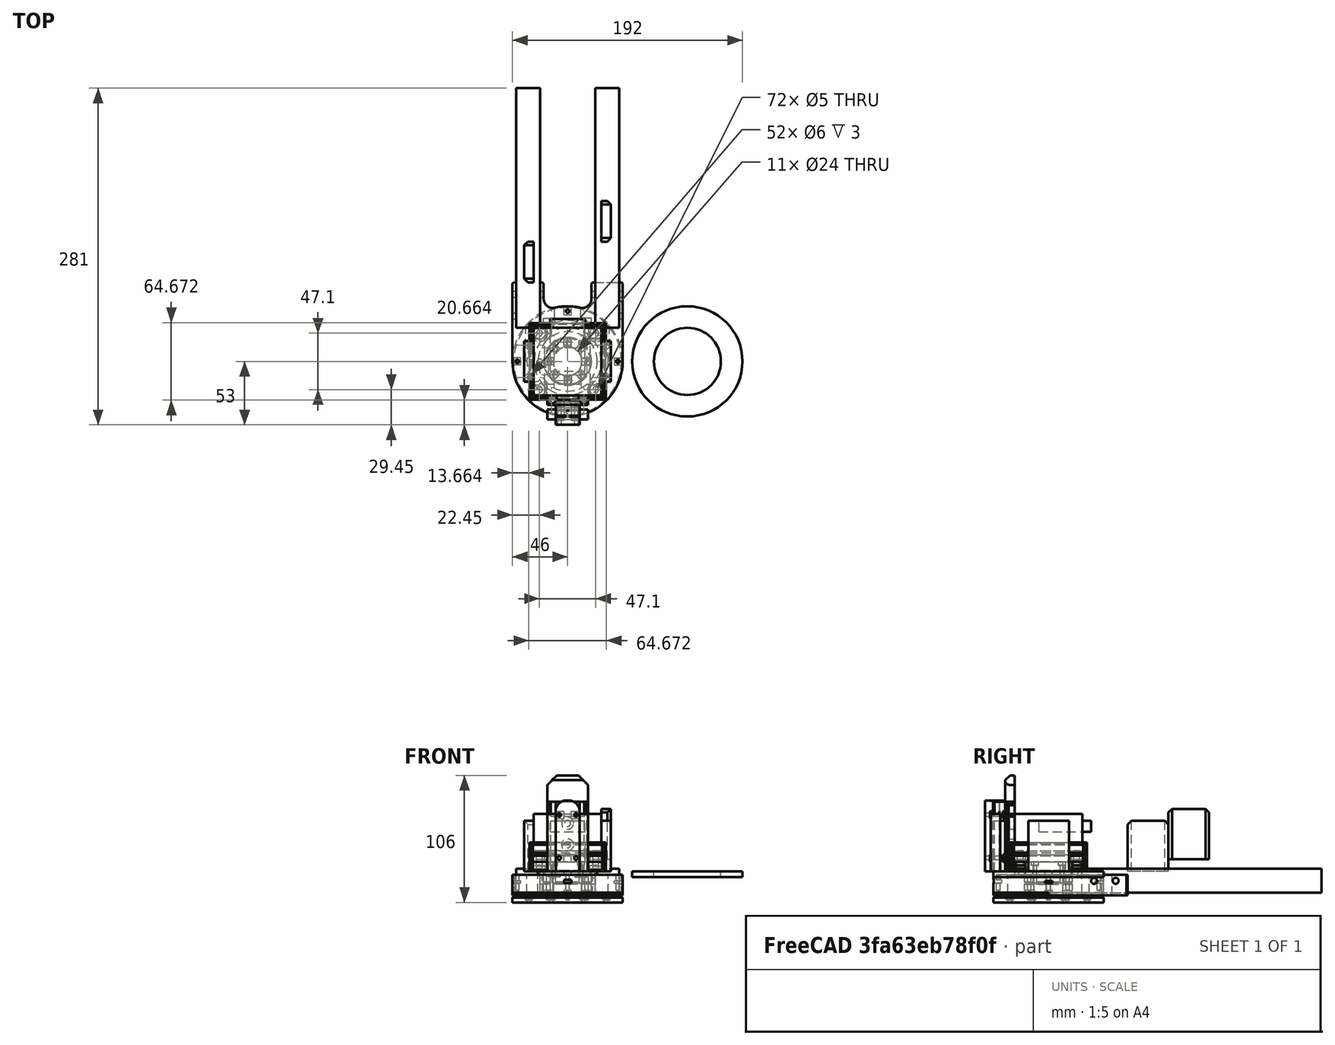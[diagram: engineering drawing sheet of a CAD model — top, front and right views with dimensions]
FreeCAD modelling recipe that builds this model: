
FCSTD DOCUMENT  (FreeCAD 0.19R24276 (Git))
Label: J-max_moto-hold_012
License: All rights reserved
LicenseURL: http://en.wikipedia.org/wiki/All_rights_reserved
objects: Part::Cylinder×298, Part::Box×162, Part::Compound×145, Part::Cut×126, Part::Chamfer×59, Part::FeaturePython×8, Mesh::Feature×7, Part::Fillet×7, Part::MultiFuse×3, Part::Mirroring×1, Part::Common×1
note: 810 computed .brp shape members not serialized (recipe doc carries the construction recipe); baked Part::Feature solids carry a one-line shape summary decoded from their .brp

FEATURE [Part::Cylinder] Cylinder116  label="Válec116"
  Angle = 360
  AttacherType = Attacher::AttachEngine3D
  Height = 20
  Placement = pos=(-13.3939,32.3358,-22) rot=(0,0,1;1.96349rad)
  Radius = 1.5
FEATURE [Part::Box] Box049  label="Krychle049"
  AttacherType = Attacher::AttachEngine3D
  Height = 2
  Length = 10
  Placement = pos=(-11,3,6) rot=(0,0,1;3.14159rad)
  Width = 6
FEATURE [Part::Cylinder] Cylinder127  label="Válec127"
  Angle = 360
  AttacherType = Attacher::AttachEngine3D
  Height = 3
  Placement = pos=(-32.3358,-13.3939,-22) rot=(0,0,1;3.53429rad)
  Radius = 3
FEATURE [Part::Cylinder] Cylinder124  label="Válec124"
  Angle = 360
  AttacherType = Attacher::AttachEngine3D
  Height = 3
  Placement = pos=(-32.3358,13.3939,-22) rot=(0,0,1;2.74889rad)
  Radius = 3
FEATURE [Part::Box] Box048  label="Krychle048"
  AttacherType = Attacher::AttachEngine3D
  Height = 2
  Length = 10
  Placement = pos=(3,11,6) rot=(0,0,1;1.5708rad)
  Width = 6
FEATURE [Part::Box] Box050  label="Krychle050"
  AttacherType = Attacher::AttachEngine3D
  Height = 2
  Length = 10
  Placement = pos=(-3,-11,6) rot=(0,0,-1;1.5708rad)
  Width = 6
FEATURE [Part::Cylinder] Cylinder131  label="Válec131"
  Angle = 360
  AttacherType = Attacher::AttachEngine3D
  Height = 16
  Placement = pos=(2e-15,16,2) rot=(0,0,-1;1.1781rad)
  Radius = 1.5
FEATURE [Part::Cylinder] Cylinder132  label="Válec132"
  Angle = 360
  AttacherType = Attacher::AttachEngine3D
  Height = 16
  Placement = pos=(-16,7e-15,2) rot=(0,0,1;0.392699rad)
  Radius = 1.5
FEATURE [Part::Cylinder] Cylinder126  label="Válec126"
  Angle = 360
  AttacherType = Attacher::AttachEngine3D
  Height = 3
  Placement = pos=(13.3939,-32.3358,-22) rot=(0,0,-1;1.1781rad)
  Radius = 3
FEATURE [Part::Cylinder] Cylinder130  label="Válec130"
  Angle = 360
  AttacherType = Attacher::AttachEngine3D
  Height = 16
  Placement = pos=(16,0,2) rot=(0,0,1;3.53429rad)
  Radius = 1.5
FEATURE [Part::Cylinder] Cylinder125  label="Válec125"
  Angle = 360
  AttacherType = Attacher::AttachEngine3D
  Height = 3
  Placement = pos=(-13.3939,-32.3358,-22) rot=(0,0,-1;1.96349rad)
  Radius = 3
FEATURE [Part::Cylinder] Cylinder128  label="Válec128"
  Angle = 360
  AttacherType = Attacher::AttachEngine3D
  Height = 3
  Placement = pos=(32.3358,13.3939,-22) rot=(0,0,1;0.392699rad)
  Radius = 3
FEATURE [Part::Cylinder] Cylinder129  label="Válec129"
  Angle = 360
  AttacherType = Attacher::AttachEngine3D
  Height = 3
  Placement = pos=(13.3939,32.3358,-22) rot=(0,0,1;1.1781rad)
  Radius = 3
FEATURE [Part::Box] Box  label="Krychle"
  AttacherType = Attacher::AttachEngine3D
  Height = 2
  Length = 10
  Placement = pos=(11,-3,6) rot=(0,0,1;0rad)
  Width = 6
FEATURE [Part::Cylinder] Cylinder122  label="Válec122"
  Angle = 360
  AttacherType = Attacher::AttachEngine3D
  Height = 3
  Placement = pos=(-13.3939,32.3358,-22) rot=(0,0,1;1.96349rad)
  Radius = 3
FEATURE [Part::Cylinder] Cylinder121  label="Válec121"
  Angle = 360
  AttacherType = Attacher::AttachEngine3D
  Height = 20
  Placement = pos=(32.3358,-13.3939,-22) rot=(0,0,-1;0.392699rad)
  Radius = 1.5
FEATURE [Part::Cylinder] Cylinder117  label="Válec117"
  Angle = 360
  AttacherType = Attacher::AttachEngine3D
  Height = 20
  Placement = pos=(-32.3358,13.3939,-22) rot=(0,0,1;2.74889rad)
  Radius = 1.5
FEATURE [Part::Cylinder] Cylinder123  label="Válec123"
  Angle = 360
  AttacherType = Attacher::AttachEngine3D
  Height = 3
  Placement = pos=(32.3358,-13.3939,-22) rot=(0,0,-1;0.392699rad)
  Radius = 3
FEATURE [Part::Cylinder] Cylinder119  label="Válec119"
  Angle = 360
  AttacherType = Attacher::AttachEngine3D
  Height = 20
  Placement = pos=(-13.3939,-32.3358,-22) rot=(0,0,-1;1.96349rad)
  Radius = 1.5
FEATURE [Part::Cylinder] Cylinder120  label="Válec120"
  Angle = 360
  AttacherType = Attacher::AttachEngine3D
  Height = 20
  Placement = pos=(13.3939,-32.3358,-22) rot=(0,0,-1;1.1781rad)
  Radius = 1.5
FEATURE [Part::Cylinder] Cylinder118  label="Válec118"
  Angle = 360
  AttacherType = Attacher::AttachEngine3D
  Height = 20
  Placement = pos=(-32.3358,-13.3939,-22) rot=(0,0,1;3.53429rad)
  Radius = 1.5
FEATURE [Part::FeaturePython] Tube009  # WARN: FeaturePython — macro-defined, semantics opaque (R4)
  AttacherType = Attacher::AttachEngine3D
  Height = 5
  InnerRadius = 12
  OuterRadius = 46
FEATURE [Part::FeaturePython] Tube010  # WARN: FeaturePython — macro-defined, semantics opaque (R4)
  AttacherType = Attacher::AttachEngine3D
  Height = 11
  InnerRadius = 12
  OuterRadius = 20
  Placement = pos=(0,0,5) rot=(0,0,1;0rad)
FEATURE [Part::Cylinder] Cylinder133  label="Válec133"
  Angle = 360
  AttacherType = Attacher::AttachEngine3D
  Height = 16
  Placement = pos=(-1.2e-14,-16,2) rot=(0,0,1;1.96349rad)
  Radius = 1.5
FEATURE [Part::Compound] Compound203
  Links = -> [Cylinder130,Cylinder131,Cylinder132,Cylinder133]
FEATURE [Part::Compound] Compound202
  Links = -> [Box,Box048,Box049,Box050]
  Placement = pos=(0,0,2) rot=(0,0,1;0rad)
FEATURE [Part::Cut] Cut
  Base = -> Tube010
  Tool = -> Compound202
FEATURE [Part::Compound] Compound204
  Links = -> [Tube009,Cut]
FEATURE [Part::Cylinder] Cylinder114  label="Válec114"
  Angle = 360
  AttacherType = Attacher::AttachEngine3D
  Height = 20
  Placement = pos=(32.3358,13.3939,-22) rot=(0,0,1;0.392699rad)
  Radius = 1.5
FEATURE [Part::Cylinder] Cylinder115  label="Válec115"
  Angle = 360
  AttacherType = Attacher::AttachEngine3D
  Height = 20
  Placement = pos=(13.3939,32.3358,-22) rot=(0,0,1;1.1781rad)
  Radius = 1.5
FEATURE [Part::Cut] Cut062
  Base = -> Compound204
  Tool = -> Compound203
FEATURE [Part::FeaturePython] Tube011  # WARN: FeaturePython — macro-defined, semantics opaque (R4)
  AttacherType = Attacher::AttachEngine3D
  Height = 3
  InnerRadius = 19
  OuterRadius = 24.8
  Placement = pos=(0,0,5) rot=(0,0,1;0rad)
FEATURE [Part::Compound] Compound
  Links = -> [Cylinder114,Cylinder115,Cylinder116,Cylinder117,Cylinder118,Cylinder119,Cylinder120,Cylinder121]
  Placement = pos=(0,0,8) rot=(0,0,1;0rad)
FEATURE [Part::Compound] Compound200
  Links = -> [Cylinder128,Cylinder129,Cylinder122,Cylinder124,Cylinder127,Cylinder125,Cylinder126,Cylinder123]
  Placement = pos=(0,0,24) rot=(0,0,1;0rad)
FEATURE [Part::Cut] Cut063
  Base = -> Cut062
  Tool = -> Compound200
FEATURE [Part::Cut] Cut064
  Base = -> Cut063
  Tool = -> Compound
FEATURE [Part::Chamfer] Chamfer
  Base = -> Cut064
  Edges = 1 edges r=1: [Edge76]
FEATURE [Part::Compound] Compound206
  Links = -> [Tube011,Chamfer]
FEATURE [Part::Chamfer] Chamfer001  label="podmotoro"
  Base = -> Compound206
  Edges = 1 edges r=1: [Edge93]
FEATURE [Part::FeaturePython] Tube  # WARN: FeaturePython — macro-defined, semantics opaque (R4)
  AttacherType = Attacher::AttachEngine3D
  Height = 10
  InnerRadius = 12
  OuterRadius = 20
  Placement = pos=(0,0,16) rot=(0,0,1;0rad)
FEATURE [Part::Cylinder] Cylinder  label="Válec"
  Angle = 360
  AttacherType = Attacher::AttachEngine3D
  Height = 15
  Placement = pos=(-23,0,8) rot=(0,0,1;0rad)
  Radius = 2
FEATURE [Part::FeaturePython] Tube012  # WARN: FeaturePython — macro-defined, semantics opaque (R4)
  AttacherType = Attacher::AttachEngine3D
  Height = 2
  InnerRadius = 28
  OuterRadius = 46
  Placement = pos=(0,0,6) rot=(0,0,1;0rad)
FEATURE [Part::FeaturePython] Tube013  # WARN: FeaturePython — macro-defined, semantics opaque (R4)
  AttacherType = Attacher::AttachEngine3D
  Height = 15
  InnerRadius = 34
  OuterRadius = 46
  Placement = pos=(0,0,8) rot=(0,0,1;0rad)
FEATURE [Part::FeaturePython] Tube014  # WARN: FeaturePython — macro-defined, semantics opaque (R4)
  AttacherType = Attacher::AttachEngine3D
  Height = 5
  InnerRadius = 28
  OuterRadius = 46
  Placement = pos=(100,0,21) rot=(0,0,1;0rad)
FEATURE [Part::FeaturePython] Tube015  # WARN: FeaturePython — macro-defined, semantics opaque (R4)
  AttacherType = Attacher::AttachEngine3D
  Height = 3
  InnerRadius = 19.5
  OuterRadius = 24.8
  Placement = pos=(0,0,23) rot=(0,0,1;0rad)
FEATURE [Part::Cylinder] Cylinder134  label="Válec134"
  Angle = 360
  AttacherType = Attacher::AttachEngine3D
  Height = 30
  Placement = pos=(16,0,2) rot=(0,0,1;3.53429rad)
  Radius = 1.5
FEATURE [Part::Cylinder] Cylinder135  label="Válec135"
  Angle = 360
  AttacherType = Attacher::AttachEngine3D
  Height = 30
  Placement = pos=(2e-15,16,2) rot=(0,0,-1;1.1781rad)
  Radius = 1.5
FEATURE [Part::Cylinder] Cylinder136  label="Válec136"
  Angle = 360
  AttacherType = Attacher::AttachEngine3D
  Height = 30
  Placement = pos=(-16,7e-15,2) rot=(0,0,1;0.392699rad)
  Radius = 1.5
FEATURE [Part::Cylinder] Cylinder137  label="Válec137"
  Angle = 360
  AttacherType = Attacher::AttachEngine3D
  Height = 30
  Placement = pos=(-1.2e-14,-16,2) rot=(0,0,1;1.96349rad)
  Radius = 1.5
FEATURE [Part::Compound] Compound208
  Links = -> [Cylinder137,Cylinder136,Cylinder135,Cylinder134]
  Placement = pos=(0,0,-2) rot=(0,0,1;0rad)
FEATURE [Part::Cylinder] Cylinder138  label="Válec138"
  Angle = 360
  AttacherType = Attacher::AttachEngine3D
  Height = 3
  Placement = pos=(-1.2e-14,-16,2) rot=(0,0,1;1.96349rad)
  Radius = 3
FEATURE [Part::Cylinder] Cylinder139  label="Válec139"
  Angle = 360
  AttacherType = Attacher::AttachEngine3D
  Height = 3
  Placement = pos=(16,0,2) rot=(0,0,1;3.53429rad)
  Radius = 3
FEATURE [Part::Cylinder] Cylinder140  label="Válec140"
  Angle = 360
  AttacherType = Attacher::AttachEngine3D
  Height = 3
  Placement = pos=(2e-15,16,2) rot=(0,0,-1;1.1781rad)
  Radius = 3
FEATURE [Part::Cylinder] Cylinder141  label="Válec141"
  Angle = 360
  AttacherType = Attacher::AttachEngine3D
  Height = 3
  Placement = pos=(-16,7e-15,2) rot=(0,0,1;0.392699rad)
  Radius = 3
FEATURE [Part::Compound] Compound209
  Links = -> [Cylinder138,Cylinder141,Cylinder140,Cylinder139]
  Placement = pos=(0,0,21) rot=(0,0,1;0rad)
FEATURE [Part::Cut] Cut065
  Base = -> Tube
  Tool = -> Compound209
FEATURE [Part::Cut] Cut066
  Base = -> Cut065
  Tool = -> Compound208
FEATURE [Part::Box] Box052  label="Krychle052"
  AttacherType = Attacher::AttachEngine3D
  Height = 20
  Length = 20
  Placement = pos=(-43,28,8) rot=(0,0,1;0rad)
  Width = 200
FEATURE [Part::Box] Box053  label="Krychle053"
  AttacherType = Attacher::AttachEngine3D
  Height = 17
  Length = 26
  Placement = pos=(20,30,6) rot=(0,0,1;0rad)
  Width = 36
FEATURE [Part::Cylinder] Cylinder142  label="Válec142"
  Angle = 360
  AttacherType = Attacher::AttachEngine3D
  Height = 20
  Placement = pos=(12,52.5,3) rot=(0,0,1;0rad)
  Radius = 8
FEATURE [Part::Box] Box054  label="Krychle054"
  AttacherType = Attacher::AttachEngine3D
  Height = 17
  Length = 32
  Placement = pos=(11,36,6) rot=(0,0,1;0rad)
  Width = 17
FEATURE [Part::Box] Box055  label="Krychle055"
  AttacherType = Attacher::AttachEngine3D
  Height = 17
  Length = 11
  Placement = pos=(35,0,6) rot=(0,0,1;0rad)
  Width = 36
FEATURE [Part::Cut] Cut067
  Base = -> Box054
  Tool = -> Cylinder142
FEATURE [Part::Box] Box051  label="Krychle051"
  AttacherType = Attacher::AttachEngine3D
  Height = 20
  Length = 20
  Placement = pos=(23,28,8) rot=(0,0,1;0rad)
  Width = 200
FEATURE [Part::MultiFuse] Fusion
  Shapes = -> [Box053,Box055,Cut067]
FEATURE [Part::Mirroring] mirror  label="Fusion (mirrored)"
  Base = (0,0,0)
  Normal = (1,0,0)
  Source = -> Fusion
FEATURE [Part::Box] Box056  label="Krychle056"
  AttacherType = Attacher::AttachEngine3D
  Height = 17
  Length = 26
  Placement = pos=(20,30,6) rot=(0,0,1;0rad)
  Width = 36
FEATURE [Part::Cylinder] Cylinder143  label="Válec143"
  Angle = 360
  AttacherType = Attacher::AttachEngine3D
  Height = 20
  Placement = pos=(12,52.5,3) rot=(0,0,1;0rad)
  Radius = 8
FEATURE [Part::Box] Box057  label="Krychle057"
  AttacherType = Attacher::AttachEngine3D
  Height = 17
  Length = 32
  Placement = pos=(11,36,6) rot=(0,0,1;0rad)
  Width = 17
FEATURE [Part::Box] Box058  label="Krychle058"
  AttacherType = Attacher::AttachEngine3D
  Height = 17
  Length = 11
  Placement = pos=(35,0,6) rot=(0,0,1;0rad)
  Width = 36
FEATURE [Part::Cut] Cut068
  Base = -> Box057
  Tool = -> Cylinder143
FEATURE [Part::MultiFuse] Fusion001
  Shapes = -> [Box056,Box058,Cut068]
FEATURE [Part::MultiFuse] Fusion002
  Shapes = -> [Tube013,mirror,Fusion001]
FEATURE [Part::Compound] Compound210
  Links = -> [Box051,Box052]
FEATURE [Part::Cut] Cut069
  Base = -> Fusion002
  Tool = -> Compound210
FEATURE [Part::Box] Box059  label="Krychle059"
  AttacherType = Attacher::AttachEngine3D
  Height = 20
  Length = 20
  Placement = pos=(23,28,8) rot=(0,0,1;0rad)
  Width = 200
FEATURE [Part::Box] Box060  label="Krychle060"
  AttacherType = Attacher::AttachEngine3D
  Height = 20
  Length = 20
  Placement = pos=(-43,28,8) rot=(0,0,1;0rad)
  Width = 200
FEATURE [Part::Cylinder] Cylinder144  label="Válec144"
  Angle = 360
  AttacherType = Attacher::AttachEngine3D
  Height = 150
  Placement = pos=(-57,56,18) rot=(0,1,0;1.5708rad)
  Radius = 2.5
FEATURE [Part::Cylinder] Cylinder145  label="Válec145"
  Angle = 360
  AttacherType = Attacher::AttachEngine3D
  Height = 30
  Placement = pos=(-57,38,18) rot=(0,1,0;1.5708rad)
  Radius = 2.5
FEATURE [Part::Cylinder] Cylinder146  label="Válec146"
  Angle = 360
  AttacherType = Attacher::AttachEngine3D
  Height = 30
  Placement = pos=(28,38,18) rot=(0,1,0;1.5708rad)
  Radius = 2.5
FEATURE [Part::Compound] Compound211
  Links = -> [Cylinder144,Cylinder145,Cylinder146]
FEATURE [Part::Cut] Cut070
  Base = -> Cut069
  Tool = -> Compound211
FEATURE [Part::Cylinder] Cylinder149  label="Válec149"
  Angle = 360
  AttacherType = Attacher::AttachEngine3D
  Height = 30
  Placement = pos=(0,42,10) rot=(0,0,-1;1.1781rad)
  Radius = 1.5
FEATURE [Part::Box] Box062  label="Krychle062"
  AttacherType = Attacher::AttachEngine3D
  Height = 2
  Length = 6
  Placement = pos=(-3,39,16) rot=(0,0,1;0rad)
  Width = 8
FEATURE [Part::Box] Box063  label="Krychle063"
  AttacherType = Attacher::AttachEngine3D
  Height = 2
  Length = 6
  Placement = pos=(-39,-3,16) rot=(0,0,1;1.5708rad)
  Width = 8
FEATURE [Part::Box] Box064  label="Krychle064"
  AttacherType = Attacher::AttachEngine3D
  Height = 3
  Length = 6
  Placement = pos=(3,-39,16) rot=(0,0,1;3.14159rad)
  Width = 8
FEATURE [Part::Box] Box065  label="Krychle065"
  AttacherType = Attacher::AttachEngine3D
  Height = 2
  Length = 6
  Placement = pos=(39,3,16) rot=(0,0,-1;1.5708rad)
  Width = 8
FEATURE [Part::Compound] Compound212
  Links = -> [Box062,Box063,Box064,Box065]
FEATURE [Part::Cut] Cut071
  Base = -> Cut070
  Tool = -> Compound212
FEATURE [Part::Cylinder] Cylinder150  label="Válec150"
  Angle = 360
  AttacherType = Attacher::AttachEngine3D
  Height = 30
  Placement = pos=(-42,-8e-15,10) rot=(0,0,1;0.392699rad)
  Radius = 1.5
FEATURE [Part::Cylinder] Cylinder151  label="Válec151"
  Angle = 360
  AttacherType = Attacher::AttachEngine3D
  Height = 30
  Placement = pos=(1.5e-14,-42,10) rot=(0,0,1;1.96349rad)
  Radius = 1.5
FEATURE [Part::Cylinder] Cylinder152  label="Válec152"
  Angle = 360
  AttacherType = Attacher::AttachEngine3D
  Height = 30
  Placement = pos=(42,3.4e-14,10) rot=(0,0,1;3.53429rad)
  Radius = 1.5
FEATURE [Part::Compound] Compound213
  Links = -> [Cylinder149,Cylinder150,Cylinder151,Cylinder152]
FEATURE [Part::Cut] Cut072
  Base = -> Cut071
  Tool = -> Compound213
FEATURE [Part::Chamfer] Chamfer002
  Base = -> Cut072
  Edges = 1 edges r=1: [Edge143]
FEATURE [Part::Chamfer] Chamfer003
  Base = -> Chamfer002
  Edges = 1 edges r=1: [Edge6]
FEATURE [Part::Chamfer] Chamfer004
  Base = -> Chamfer003
  Edges = 1 edges r=1: [Edge263]
FEATURE [Part::Chamfer] Chamfer005
  Base = -> Chamfer004
  Edges = 1 edges r=1: [Edge6]
FEATURE [Part::Compound] Compound214  label="armovadlo"
  Links = -> [Tube012,Chamfer005]
FEATURE [Mesh::Feature] Mesh  label="armovadlo (Meshed)"
FEATURE [Part::Box] Box066  label="Krychle066"
  AttacherType = Attacher::AttachEngine3D
  Height = 40
  Length = 56.5
  Placement = pos=(-28.25,-28.25,34) rot=(0,0,1;0rad)
  Width = 56.5
FEATURE [Part::Box] Box067  label="Krychle067"
  AttacherType = Attacher::AttachEngine3D
  Height = 8
  Length = 64
  Placement = pos=(-32,-32,26) rot=(0,0,1;0rad)
  Width = 64
FEATURE [Part::Cylinder] Cylinder153  label="Válec153"
  Angle = 360
  AttacherType = Attacher::AttachEngine3D
  Height = 3
  Placement = pos=(-1.2e-14,-16,2) rot=(0,0,1;1.96349rad)
  Radius = 3
FEATURE [Part::Cylinder] Cylinder154  label="Válec154"
  Angle = 360
  AttacherType = Attacher::AttachEngine3D
  Height = 3
  Placement = pos=(16,0,2) rot=(0,0,1;3.53429rad)
  Radius = 3
FEATURE [Part::Cylinder] Cylinder155  label="Válec155"
  Angle = 360
  AttacherType = Attacher::AttachEngine3D
  Height = 3
  Placement = pos=(-16,7e-15,2) rot=(0,0,1;0.392699rad)
  Radius = 3
FEATURE [Part::Cylinder] Cylinder156  label="Válec156"
  Angle = 360
  AttacherType = Attacher::AttachEngine3D
  Height = 3
  Placement = pos=(2e-15,16,2) rot=(0,0,-1;1.1781rad)
  Radius = 3
FEATURE [Part::Compound] Compound215
  Links = -> [Cylinder153,Cylinder155,Cylinder156,Cylinder154]
  Placement = pos=(0,0,29) rot=(0,0,1;0.785398rad)
FEATURE [Part::Cylinder] Cylinder157  label="Válec157"
  Angle = 360
  AttacherType = Attacher::AttachEngine3D
  Height = 30
  Placement = pos=(-1.2e-14,-16,2) rot=(0,0,1;1.96349rad)
  Radius = 1.5
FEATURE [Part::Cylinder] Cylinder158  label="Válec158"
  Angle = 360
  AttacherType = Attacher::AttachEngine3D
  Height = 30
  Placement = pos=(16,0,2) rot=(0,0,1;3.53429rad)
  Radius = 1.5
FEATURE [Part::Cylinder] Cylinder159  label="Válec159"
  Angle = 360
  AttacherType = Attacher::AttachEngine3D
  Height = 30
  Placement = pos=(2e-15,16,2) rot=(0,0,-1;1.1781rad)
  Radius = 1.5
FEATURE [Part::Cylinder] Cylinder160  label="Válec160"
  Angle = 360
  AttacherType = Attacher::AttachEngine3D
  Height = 30
  Placement = pos=(-16,7e-15,2) rot=(0,0,1;0.392699rad)
  Radius = 1.5
FEATURE [Part::Compound] Compound216
  Links = -> [Cylinder157,Cylinder160,Cylinder159,Cylinder158]
  Placement = pos=(0,0,-2) rot=(0,0,1;0.785398rad)
FEATURE [Part::Box] Box068  label="Krychle068"
  AttacherType = Attacher::AttachEngine3D
  Height = 2
  Length = 10
  Placement = pos=(-11,3,6) rot=(0,0,1;3.14159rad)
  Width = 6
FEATURE [Part::Box] Box069  label="Krychle069"
  AttacherType = Attacher::AttachEngine3D
  Height = 2
  Length = 10
  Placement = pos=(3,11,6) rot=(0,0,1;1.5708rad)
  Width = 6
FEATURE [Part::Box] Box070  label="Krychle070"
  AttacherType = Attacher::AttachEngine3D
  Height = 2
  Length = 10
  Placement = pos=(11,-3,6) rot=(0,0,1;0rad)
  Width = 6
FEATURE [Part::Box] Box071  label="Krychle071"
  AttacherType = Attacher::AttachEngine3D
  Height = 2
  Length = 10
  Placement = pos=(-3,-11,6) rot=(0,0,-1;1.5708rad)
  Width = 6
FEATURE [Part::Compound] Compound217
  Links = -> [Box070,Box069,Box068,Box071]
  Placement = pos=(0,0,15) rot=(0,0,1;0.785398rad)
FEATURE [Part::Cut] Cut073
  Base = -> Cut066
  Tool = -> Compound217
FEATURE [Part::Cut] Cut074
  Base = -> Cut073
  Tool = -> Compound216
FEATURE [Part::Cylinder] Cylinder161  label="Válec161"
  Angle = 360
  AttacherType = Attacher::AttachEngine3D
  Height = 30
  Placement = pos=(-1.2e-14,-16,2) rot=(0,0,1;1.96349rad)
  Radius = 1.5
FEATURE [Part::Cylinder] Cylinder162  label="Válec162"
  Angle = 360
  AttacherType = Attacher::AttachEngine3D
  Height = 30
  Placement = pos=(16,0,2) rot=(0,0,1;3.53429rad)
  Radius = 1.5
FEATURE [Part::Cylinder] Cylinder163  label="Válec163"
  Angle = 360
  AttacherType = Attacher::AttachEngine3D
  Height = 30
  Placement = pos=(2e-15,16,2) rot=(0,0,-1;1.1781rad)
  Radius = 1.5
FEATURE [Part::Cylinder] Cylinder164  label="Válec164"
  Angle = 360
  AttacherType = Attacher::AttachEngine3D
  Height = 30
  Placement = pos=(-16,7e-15,2) rot=(0,0,1;0.392699rad)
  Radius = 1.5
FEATURE [Part::Compound] Compound218
  Links = -> [Cylinder161,Cylinder164,Cylinder163,Cylinder162]
  Placement = pos=(0,0,14) rot=(0,0,1;0.785398rad)
FEATURE [Part::Compound] Compound219
  Links = -> [Tube015,Cut074]
FEATURE [Part::Chamfer] Chamfer006
  Base = -> Compound219
  Edges = 1 edges r=1: [Edge8]
FEATURE [Mesh::Feature] Mesh001  label="Chamfer006 (Meshed)"
FEATURE [Part::Cut] Cut075
  Base = -> Box067
  Tool = -> Compound218
FEATURE [Part::Cut] Cut076
  Base = -> Cut075
  Tool = -> Compound215
FEATURE [Part::Cylinder] Cylinder165  label="Válec165"
  Angle = 360
  AttacherType = Attacher::AttachEngine3D
  Height = 20
  Placement = pos=(23.55,23.55,20) rot=(0,0,1;0rad)
  Radius = 2.5
FEATURE [Part::Cylinder] Cylinder166  label="Válec166"
  Angle = 360
  AttacherType = Attacher::AttachEngine3D
  Height = 20
  Placement = pos=(23.55,-23.55,20) rot=(0,0,1;0rad)
  Radius = 2.5
FEATURE [Part::Cylinder] Cylinder167  label="Válec167"
  Angle = 360
  AttacherType = Attacher::AttachEngine3D
  Height = 20
  Placement = pos=(-23.55,-23.55,20) rot=(0,0,1;0rad)
  Radius = 2.5
FEATURE [Part::Cylinder] Cylinder168  label="Válec168"
  Angle = 360
  AttacherType = Attacher::AttachEngine3D
  Height = 20
  Placement = pos=(-23.55,23.55,20) rot=(0,0,1;0rad)
  Radius = 2.5
FEATURE [Part::Compound] Compound220
  Links = -> [Cylinder165,Cylinder168,Cylinder167,Cylinder166]
FEATURE [Part::Cut] Cut077
  Base = -> Cut076
  Tool = -> Compound220
FEATURE [Part::Cylinder] Cylinder169  label="Válec169"
  Angle = 360
  AttacherType = Attacher::AttachEngine3D
  Height = 4
  Placement = pos=(-23.55,-23.55,26) rot=(0,0,1;0rad)
  Radius = 5
FEATURE [Part::Cylinder] Cylinder170  label="Válec170"
  Angle = 360
  AttacherType = Attacher::AttachEngine3D
  Height = 4
  Placement = pos=(23.55,23.55,26) rot=(0,0,1;0rad)
  Radius = 5
FEATURE [Part::Cylinder] Cylinder171  label="Válec171"
  Angle = 360
  AttacherType = Attacher::AttachEngine3D
  Height = 4
  Placement = pos=(23.55,-23.55,26) rot=(0,0,1;0rad)
  Radius = 5
FEATURE [Part::Cylinder] Cylinder172  label="Válec172"
  Angle = 360
  AttacherType = Attacher::AttachEngine3D
  Height = 4
  Placement = pos=(-23.55,23.55,26) rot=(0,0,1;0rad)
  Radius = 5
FEATURE [Part::Compound] Compound221
  Links = -> [Cylinder169,Cylinder170,Cylinder171,Cylinder172]
FEATURE [Part::Cut] Cut078
  Base = -> Cut077
  Tool = -> Compound221
FEATURE [Part::Box] Box072  label="Krychle072"
  AttacherType = Attacher::AttachEngine3D
  Height = 16
  Length = 64
  Placement = pos=(-32,-32,34) rot=(0,0,1;0rad)
  Width = 64
FEATURE [Part::Box] Box073  label="Krychle073"
  AttacherType = Attacher::AttachEngine3D
  Height = 40
  Length = 56.5
  Placement = pos=(-28.25,-28.25,34) rot=(0,0,1;0rad)
  Width = 56.5
FEATURE [Part::Cut] Cut079
  Base = -> Box072
  Tool = -> Box066
FEATURE [Part::Cylinder] Cylinder173  label="Válec173"
  Angle = 360
  AttacherType = Attacher::AttachEngine3D
  Height = 20
  Placement = pos=(0,0,15) rot=(0,0,1;0rad)
  Radius = 12
FEATURE [Part::Cut] Cut080
  Base = -> Cut078
  Tool = -> Cylinder173
FEATURE [Part::Box] Box074  label="Krychle074"
  AttacherType = Attacher::AttachEngine3D
  Height = 58
  Length = 34
  Placement = pos=(-17,-36.25,26) rot=(0,0,1;0rad)
  Width = 8
FEATURE [Part::Box] Box075  label="Krychle075"
  AttacherType = Attacher::AttachEngine3D
  Height = 48
  Length = 34
  Placement = pos=(-17,-48.25,26) rot=(0,0,1;0rad)
  Width = 8
FEATURE [Part::Cylinder] Cylinder174  label="Válec174"
  Angle = 360
  AttacherType = Attacher::AttachEngine3D
  Height = 12
  Placement = pos=(0,-32.55,100) rot=(0.57735,-0.57735,-0.57735;4.18879rad)
  Radius = 5
FEATURE [Part::Cylinder] Cylinder175  label="Válec175"
  Angle = 360
  AttacherType = Attacher::AttachEngine3D
  Height = 12
  Placement = pos=(0,-32.55,100) rot=(0,1,0;1.5708rad)
  Radius = 5
FEATURE [Part::Cylinder] Cylinder177  label="Válec177"
  Angle = 360
  AttacherType = Attacher::AttachEngine3D
  Height = 50
  Placement = pos=(0,100,66) rot=(0,1,0;1.5708rad)
  Radius = 2.5
FEATURE [Part::Compound] Compound222
  Links = -> [Cylinder177]
  Placement = pos=(0,0,100) rot=(0,0,1;0rad)
FEATURE [Part::Compound] Compound223
  Links = -> [Cylinder174,Cylinder175]
FEATURE [Part::Cut] Cut081
  Base = -> Box074
  Tool = -> Compound222
FEATURE [Part::Cut] Cut082
  Base = -> Cut081
  Tool = -> Compound223
FEATURE [Part::Compound] Compound224  label="hrubo_holder"
  Links = -> [Cut080,Cut082,Cut079]
FEATURE [Part::Box] Box076  label="Krychle076"
  AttacherType = Attacher::AttachEngine3D
  Height = 48
  Length = 34
  Placement = pos=(-17,-36.25,26) rot=(0,0,1;0rad)
  Width = 8
FEATURE [Part::Box] Box077  label="Krychle077"
  AttacherType = Attacher::AttachEngine3D
  Height = 40
  Length = 56.5
  Placement = pos=(-28.25,-28.25,34) rot=(0,0,1;0rad)
  Width = 56.5
FEATURE [Part::Box] Box078  label="Krychle078"
  AttacherType = Attacher::AttachEngine3D
  Height = 8
  Length = 64
  Placement = pos=(-32,-32,26) rot=(0,0,1;0rad)
  Width = 64
FEATURE [Part::Cylinder] Cylinder179  label="Válec179"
  Angle = 360
  AttacherType = Attacher::AttachEngine3D
  Height = 20
  Placement = pos=(0,0,15) rot=(0,0,1;0rad)
  Radius = 12
FEATURE [Part::Cylinder] Cylinder180  label="Válec180"
  Angle = 360
  AttacherType = Attacher::AttachEngine3D
  Height = 3
  Placement = pos=(2e-15,16,2) rot=(0,0,-1;1.1781rad)
  Radius = 3
FEATURE [Part::Cylinder] Cylinder181  label="Válec181"
  Angle = 360
  AttacherType = Attacher::AttachEngine3D
  Height = 3
  Placement = pos=(-1.2e-14,-16,2) rot=(0,0,1;1.96349rad)
  Radius = 3
FEATURE [Part::Cylinder] Cylinder182  label="Válec182"
  Angle = 360
  AttacherType = Attacher::AttachEngine3D
  Height = 3
  Placement = pos=(-16,7e-15,2) rot=(0,0,1;0.392699rad)
  Radius = 3
FEATURE [Part::Cylinder] Cylinder183  label="Válec183"
  Angle = 360
  AttacherType = Attacher::AttachEngine3D
  Height = 3
  Placement = pos=(16,0,2) rot=(0,0,1;3.53429rad)
  Radius = 3
FEATURE [Part::Compound] Compound227
  Links = -> [Cylinder181,Cylinder182,Cylinder180,Cylinder183]
  Placement = pos=(0,0,29) rot=(0,0,1;0.785398rad)
FEATURE [Part::Cylinder] Cylinder185  label="Válec185"
  Angle = 360
  AttacherType = Attacher::AttachEngine3D
  Height = 50
  Placement = pos=(0,-54.55,66) rot=(0.57735,-0.57735,-0.57735;4.18879rad)
  Radius = 2.5
FEATURE [Part::Cylinder] Cylinder186  label="Válec186"
  Angle = 360
  AttacherType = Attacher::AttachEngine3D
  Height = 50
  Placement = pos=(0,-54.55,48) rot=(0.57735,-0.57735,-0.57735;4.18879rad)
  Radius = 2.5
FEATURE [Part::Compound] Compound228
  Links = -> [Cylinder186,Cylinder185]
FEATURE [Part::Cut] Cut084
  Base = -> Box076
  Tool = -> Compound228
FEATURE [Part::Cylinder] Cylinder187  label="Válec187"
  Angle = 360
  AttacherType = Attacher::AttachEngine3D
  Height = 20
  Placement = pos=(23.55,-23.55,20) rot=(0,0,1;0rad)
  Radius = 2.5
FEATURE [Part::Cylinder] Cylinder188  label="Válec188"
  Angle = 360
  AttacherType = Attacher::AttachEngine3D
  Height = 4
  Placement = pos=(-23.55,-23.55,26) rot=(0,0,1;0rad)
  Radius = 5
FEATURE [Part::Cylinder] Cylinder189  label="Válec189"
  Angle = 360
  AttacherType = Attacher::AttachEngine3D
  Height = 4
  Placement = pos=(23.55,-23.55,26) rot=(0,0,1;0rad)
  Radius = 5
FEATURE [Part::Cylinder] Cylinder190  label="Válec190"
  Angle = 360
  AttacherType = Attacher::AttachEngine3D
  Height = 30
  Placement = pos=(-1.2e-14,-16,2) rot=(0,0,1;1.96349rad)
  Radius = 1.5
FEATURE [Part::Cylinder] Cylinder191  label="Válec191"
  Angle = 360
  AttacherType = Attacher::AttachEngine3D
  Height = 30
  Placement = pos=(2e-15,16,2) rot=(0,0,-1;1.1781rad)
  Radius = 1.5
FEATURE [Part::Cylinder] Cylinder192  label="Válec192"
  Angle = 360
  AttacherType = Attacher::AttachEngine3D
  Height = 30
  Placement = pos=(-16,7e-15,2) rot=(0,0,1;0.392699rad)
  Radius = 1.5
FEATURE [Part::Cylinder] Cylinder193  label="Válec193"
  Angle = 360
  AttacherType = Attacher::AttachEngine3D
  Height = 4
  Placement = pos=(23.55,23.55,26) rot=(0,0,1;0rad)
  Radius = 5
FEATURE [Part::Cylinder] Cylinder194  label="Válec194"
  Angle = 360
  AttacherType = Attacher::AttachEngine3D
  Height = 20
  Placement = pos=(23.55,23.55,20) rot=(0,0,1;0rad)
  Radius = 2.5
FEATURE [Part::Cylinder] Cylinder195  label="Válec195"
  Angle = 360
  AttacherType = Attacher::AttachEngine3D
  Height = 20
  Placement = pos=(-23.55,-23.55,20) rot=(0,0,1;0rad)
  Radius = 2.5
FEATURE [Part::Cylinder] Cylinder196  label="Válec196"
  Angle = 360
  AttacherType = Attacher::AttachEngine3D
  Height = 30
  Placement = pos=(16,0,2) rot=(0,0,1;3.53429rad)
  Radius = 1.5
FEATURE [Part::Compound] Compound230
  Links = -> [Cylinder190,Cylinder192,Cylinder191,Cylinder196]
  Placement = pos=(0,0,14) rot=(0,0,1;0.785398rad)
FEATURE [Part::Cut] Cut087
  Base = -> Box078
  Tool = -> Compound230
FEATURE [Part::Cut] Cut089
  Base = -> Cut087
  Tool = -> Compound227
FEATURE [Part::Cylinder] Cylinder197  label="Válec197"
  Angle = 360
  AttacherType = Attacher::AttachEngine3D
  Height = 4
  Placement = pos=(-23.55,23.55,26) rot=(0,0,1;0rad)
  Radius = 5
FEATURE [Part::Compound] Compound229
  Links = -> [Cylinder188,Cylinder193,Cylinder189,Cylinder197]
FEATURE [Part::Box] Box079  label="Krychle079"
  AttacherType = Attacher::AttachEngine3D
  Height = 6
  Length = 64
  Placement = pos=(-32,-32,34) rot=(0,0,1;0rad)
  Width = 64
FEATURE [Part::Cut] Cut088
  Base = -> Box079
  Tool = -> Box077
FEATURE [Part::Cylinder] Cylinder198  label="Válec198"
  Angle = 360
  AttacherType = Attacher::AttachEngine3D
  Height = 20
  Placement = pos=(-23.55,23.55,20) rot=(0,0,1;0rad)
  Radius = 2.5
FEATURE [Part::Compound] Compound231
  Links = -> [Cylinder194,Cylinder198,Cylinder195,Cylinder187]
FEATURE [Part::Cut] Cut086
  Base = -> Cut089
  Tool = -> Compound231
FEATURE [Part::Cut] Cut083
  Base = -> Cut086
  Tool = -> Compound229
FEATURE [Part::Cut] Cut085
  Base = -> Cut083
  Tool = -> Cylinder179
FEATURE [Mesh::Feature] Mesh002  label="moto-holdo (Meshed)"
FEATURE [Mesh::Feature] Mesh003  label="finalo_filetovane (Meshed)"
  Placement = pos=(-200,1700,0) rot=(0,0,-1;1.5708rad)
FEATURE [Part::Box] Box080  label="Krychle080"
  AttacherType = Attacher::AttachEngine3D
  Height = 58
  Length = 20
  Placement = pos=(-10,-46.25,26) rot=(0,0,1;0rad)
  Width = 10
FEATURE [Part::Cylinder] Cylinder178  label="Válec178"
  Angle = 360
  AttacherType = Attacher::AttachEngine3D
  Height = 12
  Placement = pos=(0,-32.55,48) rot=(0.57735,-0.57735,-0.57735;4.18879rad)
  Radius = 5
FEATURE [Part::Cylinder] Cylinder184  label="Válec184"
  Angle = 360
  AttacherType = Attacher::AttachEngine3D
  Height = 12
  Placement = pos=(0,-32.55,66) rot=(0.57735,-0.57735,-0.57735;4.18879rad)
  Radius = 5
FEATURE [Part::Compound] Compound226
  Links = -> [Cylinder178,Cylinder184]
FEATURE [Part::Cut] Cut090
  Base = -> Cut084
  Tool = -> Compound226
FEATURE [Part::Compound] Compound225  label="holder"
  Links = -> [Cut085,Cut090,Cut088]
FEATURE [Part::Chamfer] Chamfer007
  Base = -> Compound225
  Edges = 2 edges r=2: [Edge20,Edge102]
FEATURE [Part::Chamfer] Chamfer008
  Base = -> Chamfer007
  Edges = 2 edges r=2: [Edge16,Edge77]
FEATURE [Part::Chamfer] Chamfer009
  Base = -> Chamfer008
  Edges = 2 edges r=2: [Edge25,Edge89]
FEATURE [Part::Chamfer] Chamfer010
  Base = -> Chamfer009
  Edges = 2 edges r=2: [Edge18,Edge92]
FEATURE [Part::Chamfer] Chamfer011
  Base = -> Chamfer010
  Edges = 1 edges r=3: [Edge118]
FEATURE [Part::Chamfer] Chamfer012
  Base = -> Chamfer011
  Edges = 1 edges r=3: [Edge2]
FEATURE [Part::Chamfer] Chamfer013
  Base = -> Chamfer012
  Edges = 1 edges r=2: [Edge3]
FEATURE [Part::Chamfer] Chamfer014
  Base = -> Chamfer013
  Edges = 1 edges r=1: [Edge113]
FEATURE [Part::Chamfer] Chamfer015
  Base = -> Chamfer014
  Edges = 1 edges r=1: [Edge6]
FEATURE [Part::Chamfer] Chamfer016
  Base = -> Chamfer015
  Edges = 1 edges r=1: [Edge3]
FEATURE [Part::Chamfer] Chamfer017
  Base = -> Chamfer016
  Edges = 1 edges r=1: [Edge3]
FEATURE [Part::Chamfer] Chamfer018
  Base = -> Chamfer017
  Edges = 1 edges r=2: [Edge69]
FEATURE [Part::Chamfer] Chamfer019
  Base = -> Chamfer018
  Edges = 1 edges r=2: [Edge23]
FEATURE [Part::Chamfer] Chamfer020
  Base = -> Chamfer019
  Edges = 1 edges r=1: [Edge116]
FEATURE [Part::Chamfer] Chamfer021
  Base = -> Chamfer020
  Edges = 1 edges r=1: [Edge8]
FEATURE [Part::Chamfer] Chamfer022
  Base = -> Chamfer021
  Edges = 1 edges r=1: [Edge34]
FEATURE [Part::Chamfer] Chamfer023  label="moto-holdo"
  Base = -> Chamfer022
  Edges = 1 edges r=1: [Edge6]
FEATURE [Part::Compound] Compound232  label="hrubo_holder2"
  Links = -> [Box080,Compound224]
FEATURE [Part::Cylinder] Cylinder199  label="Válec199"
  Angle = 360
  AttacherType = Attacher::AttachEngine3D
  Height = 12
  Placement = pos=(0,-32.55,100) rot=(0.57735,-0.57735,-0.57735;4.18879rad)
  Radius = 5
FEATURE [Part::Box] Box081  label="Krychle081"
  AttacherType = Attacher::AttachEngine3D
  Height = 48
  Length = 34
  Placement = pos=(-17,-36.25,26) rot=(0,0,1;0rad)
  Width = 8
FEATURE [Part::Box] Box082  label="Krychle082"
  AttacherType = Attacher::AttachEngine3D
  Height = 40
  Length = 56.5
  Placement = pos=(-28.25,-28.25,34) rot=(0,0,1;0rad)
  Width = 56.5
FEATURE [Part::Box] Box083  label="Krychle083"
  AttacherType = Attacher::AttachEngine3D
  Height = 8
  Length = 64
  Placement = pos=(-32,-32,26) rot=(0,0,1;0rad)
  Width = 64
FEATURE [Part::Cylinder] Cylinder200  label="Válec200"
  Angle = 360
  AttacherType = Attacher::AttachEngine3D
  Height = 20
  Placement = pos=(0,0,15) rot=(0,0,1;0rad)
  Radius = 12
FEATURE [Part::Cylinder] Cylinder201  label="Válec201"
  Angle = 360
  AttacherType = Attacher::AttachEngine3D
  Height = 3
  Placement = pos=(2e-15,16,2) rot=(0,0,-1;1.1781rad)
  Radius = 3
FEATURE [Part::Cylinder] Cylinder202  label="Válec202"
  Angle = 360
  AttacherType = Attacher::AttachEngine3D
  Height = 3
  Placement = pos=(-1.2e-14,-16,2) rot=(0,0,1;1.96349rad)
  Radius = 3
FEATURE [Part::Cylinder] Cylinder203  label="Válec203"
  Angle = 360
  AttacherType = Attacher::AttachEngine3D
  Height = 3
  Placement = pos=(-16,7e-15,2) rot=(0,0,1;0.392699rad)
  Radius = 3
FEATURE [Part::Cylinder] Cylinder204  label="Válec204"
  Angle = 360
  AttacherType = Attacher::AttachEngine3D
  Height = 3
  Placement = pos=(16,0,2) rot=(0,0,1;3.53429rad)
  Radius = 3
FEATURE [Part::Compound] Compound235
  Links = -> [Cylinder202,Cylinder203,Cylinder201,Cylinder204]
  Placement = pos=(0,0,29) rot=(0,0,1;0.785398rad)
FEATURE [Part::Cylinder] Cylinder205  label="Válec205"
  Angle = 360
  AttacherType = Attacher::AttachEngine3D
  Height = 12
  Placement = pos=(0,-32.55,100) rot=(0,1,0;1.5708rad)
  Radius = 5
FEATURE [Part::Compound] Compound234
  Links = -> [Cylinder199,Cylinder205]
FEATURE [Part::Cylinder] Cylinder206  label="Válec206"
  Angle = 360
  AttacherType = Attacher::AttachEngine3D
  Height = 50
  Placement = pos=(0,100,66) rot=(0,1,0;1.5708rad)
  Radius = 2.5
FEATURE [Part::Cylinder] Cylinder207  label="Válec207"
  Angle = 360
  AttacherType = Attacher::AttachEngine3D
  Height = 50
  Placement = pos=(0,100,48) rot=(0,1,0;1.5708rad)
  Radius = 2.5
FEATURE [Part::Compound] Compound236
  Links = -> [Cylinder207,Cylinder206]
  Placement = pos=(0,0,100) rot=(0,0,1;0rad)
FEATURE [Part::Cut] Cut092
  Base = -> Box081
  Tool = -> Compound236
FEATURE [Part::Box] Box084  label="Krychle084"
  AttacherType = Attacher::AttachEngine3D
  Height = 42
  Length = 20
  Placement = pos=(-10,-46,26) rot=(0,0,1;0rad)
  Width = 10
FEATURE [Part::Cut] Cut098
  Base = -> Cut092
  Tool = -> Compound234
FEATURE [Part::Cylinder] Cylinder208  label="Válec208"
  Angle = 360
  AttacherType = Attacher::AttachEngine3D
  Height = 20
  Placement = pos=(23.55,-23.55,20) rot=(0,0,1;0rad)
  Radius = 2.5
FEATURE [Part::Cylinder] Cylinder209  label="Válec209"
  Angle = 360
  AttacherType = Attacher::AttachEngine3D
  Height = 4
  Placement = pos=(-23.55,-23.55,26) rot=(0,0,1;0rad)
  Radius = 5
FEATURE [Part::Cylinder] Cylinder210  label="Válec210"
  Angle = 360
  AttacherType = Attacher::AttachEngine3D
  Height = 4
  Placement = pos=(23.55,-23.55,26) rot=(0,0,1;0rad)
  Radius = 5
FEATURE [Part::Cylinder] Cylinder211  label="Válec211"
  Angle = 360
  AttacherType = Attacher::AttachEngine3D
  Height = 30
  Placement = pos=(-1.2e-14,-16,2) rot=(0,0,1;1.96349rad)
  Radius = 1.5
FEATURE [Part::Cylinder] Cylinder212  label="Válec212"
  Angle = 360
  AttacherType = Attacher::AttachEngine3D
  Height = 30
  Placement = pos=(2e-15,16,2) rot=(0,0,-1;1.1781rad)
  Radius = 1.5
FEATURE [Part::Cylinder] Cylinder213  label="Válec213"
  Angle = 360
  AttacherType = Attacher::AttachEngine3D
  Height = 30
  Placement = pos=(-16,7e-15,2) rot=(0,0,1;0.392699rad)
  Radius = 1.5
FEATURE [Part::Cylinder] Cylinder214  label="Válec214"
  Angle = 360
  AttacherType = Attacher::AttachEngine3D
  Height = 4
  Placement = pos=(23.55,23.55,26) rot=(0,0,1;0rad)
  Radius = 5
FEATURE [Part::Cylinder] Cylinder215  label="Válec215"
  Angle = 360
  AttacherType = Attacher::AttachEngine3D
  Height = 20
  Placement = pos=(23.55,23.55,20) rot=(0,0,1;0rad)
  Radius = 2.5
FEATURE [Part::Cylinder] Cylinder216  label="Válec216"
  Angle = 360
  AttacherType = Attacher::AttachEngine3D
  Height = 20
  Placement = pos=(-23.55,-23.55,20) rot=(0,0,1;0rad)
  Radius = 2.5
FEATURE [Part::Cylinder] Cylinder217  label="Válec217"
  Angle = 360
  AttacherType = Attacher::AttachEngine3D
  Height = 30
  Placement = pos=(16,0,2) rot=(0,0,1;3.53429rad)
  Radius = 1.5
FEATURE [Part::Compound] Compound238
  Links = -> [Cylinder211,Cylinder213,Cylinder212,Cylinder217]
  Placement = pos=(0,0,14) rot=(0,0,1;0.785398rad)
FEATURE [Part::Cut] Cut095
  Base = -> Box083
  Tool = -> Compound238
FEATURE [Part::Cut] Cut097
  Base = -> Cut095
  Tool = -> Compound235
FEATURE [Part::Cylinder] Cylinder218  label="Válec218"
  Angle = 360
  AttacherType = Attacher::AttachEngine3D
  Height = 4
  Placement = pos=(-23.55,23.55,26) rot=(0,0,1;0rad)
  Radius = 5
FEATURE [Part::Compound] Compound237
  Links = -> [Cylinder209,Cylinder214,Cylinder210,Cylinder218]
FEATURE [Part::Box] Box085  label="Krychle085"
  AttacherType = Attacher::AttachEngine3D
  Height = 6
  Length = 64
  Placement = pos=(-32,-32,34) rot=(0,0,1;0rad)
  Width = 64
FEATURE [Part::Cut] Cut096
  Base = -> Box085
  Tool = -> Box082
FEATURE [Part::Cylinder] Cylinder219  label="Válec219"
  Angle = 360
  AttacherType = Attacher::AttachEngine3D
  Height = 20
  Placement = pos=(-23.55,23.55,20) rot=(0,0,1;0rad)
  Radius = 2.5
FEATURE [Part::Compound] Compound239
  Links = -> [Cylinder215,Cylinder219,Cylinder216,Cylinder208]
FEATURE [Part::Cut] Cut094
  Base = -> Cut097
  Tool = -> Compound239
FEATURE [Part::Cut] Cut091
  Base = -> Cut094
  Tool = -> Compound237
FEATURE [Part::Cut] Cut093
  Base = -> Cut091
  Tool = -> Cylinder200
FEATURE [Part::Compound] Compound233  label="hrubo_holder003"
  Links = -> [Cut093,Cut098,Cut096]
FEATURE [Part::Compound] Compound240  label="moto_holdo2"
  Links = -> [Box084,Compound233]
FEATURE [Part::Box] Box086  label="Krychle086"
  AttacherType = Attacher::AttachEngine3D
  Height = 20
  Length = 28.77
  Placement = pos=(-14.38,-8,34) rot=(0,0,1;0rad)
  Width = 43.38
FEATURE [Part::Cut] Cut099
  Base = -> Compound232
  Placement = pos=(-29,18,30) rot=(0,0,1;0rad)
  Tool = -> Box086
FEATURE [Part::Box] Box087  label="Krychle087"
  AttacherType = Attacher::AttachEngine3D
  Height = 9
  Length = 14.62
  Placement = pos=(-58,38,63) rot=(0,0,1;0rad)
  Width = 10
FEATURE [Part::Box] Box088  label="Krychle088"
  AttacherType = Attacher::AttachEngine3D
  Height = 9
  Length = 38
  Placement = pos=(-48,-10,63) rot=(0,0,1;0rad)
  Width = 10
FEATURE [Part::Box] Box090  label="Krychle090"
  AttacherType = Attacher::AttachEngine3D
  Height = 9
  Length = 14.62
  Placement = pos=(-14.615,38,63) rot=(0,0,1;0rad)
  Width = 10
FEATURE [Part::Box] Box091  label="Krychle091"
  AttacherType = Attacher::AttachEngine3D
  Height = 9
  Length = 10
  Placement = pos=(-58,-10,63) rot=(0,0,1;0rad)
  Width = 48
FEATURE [Part::Box] Box092  label="Krychle092"
  AttacherType = Attacher::AttachEngine3D
  Height = 9
  Length = 10
  Placement = pos=(-10,-10,63) rot=(0,0,1;0rad)
  Width = 48
FEATURE [Part::Compound] Compound241
  Links = -> [Cut099]
  Placement = pos=(29,-18,-30) rot=(0,0,1;0rad)
FEATURE [Part::Cylinder] Cylinder220  label="Válec220"
  Angle = 360
  AttacherType = Attacher::AttachEngine3D
  Height = 50
  Placement = pos=(23.55,23.55,20) rot=(0,0,1;0rad)
  Radius = 2.5
FEATURE [Part::Cylinder] Cylinder221  label="Válec221"
  Angle = 360
  AttacherType = Attacher::AttachEngine3D
  Height = 50
  Placement = pos=(-23.55,23.55,20) rot=(0,0,1;0rad)
  Radius = 2.5
FEATURE [Part::Cylinder] Cylinder222  label="Válec222"
  Angle = 360
  AttacherType = Attacher::AttachEngine3D
  Height = 50
  Placement = pos=(-23.55,-23.55,20) rot=(0,0,1;0rad)
  Radius = 2.5
FEATURE [Part::Cylinder] Cylinder223  label="Válec223"
  Angle = 360
  AttacherType = Attacher::AttachEngine3D
  Height = 50
  Placement = pos=(23.55,-23.55,20) rot=(0,0,1;0rad)
  Radius = 2.5
FEATURE [Part::Compound] Compound242
  Links = -> [Cylinder220,Cylinder223,Cylinder222,Cylinder221]
FEATURE [Part::Compound] Compound243
  Links = -> [Box087,Box092,Box091,Box090,Box088]
  Placement = pos=(29,-19,-4) rot=(0,0,1;0rad)
FEATURE [Part::Cut] Cut100
  Base = -> Compound243
  Placement = pos=(0,0,-25) rot=(0,0,1;0rad)
  Tool = -> Compound242
FEATURE [Part::Compound] Compound244  label="hrubo_holder_nuovo"
  Links = -> [Compound241,Cut100]
FEATURE [Part::Box] Box094  label="Krychle094"
  AttacherType = Attacher::AttachEngine3D
  Height = 42
  Length = 34
  Placement = pos=(36.25,-17,26) rot=(0,0,1;1.5708rad)
  Width = 8
FEATURE [Part::Box] Box095  label="Krychle095"
  AttacherType = Attacher::AttachEngine3D
  Height = 42
  Length = 34
  Placement = pos=(-36.25,17,26) rot=(0,0,-1;1.5708rad)
  Width = 8
FEATURE [Part::Compound] Compound245  label="hrubo_holder3"
  Links = -> [Box094,Box095,Cut100,Compound244]
FEATURE [Part::Cylinder] Cylinder224  label="Válec224"
  Angle = 360
  AttacherType = Attacher::AttachEngine3D
  Height = 12
  Placement = pos=(0,-32.55,100) rot=(0.57735,-0.57735,-0.57735;4.18879rad)
  Radius = 5
FEATURE [Part::Box] Box096  label="Krychle096"
  AttacherType = Attacher::AttachEngine3D
  Height = 58
  Length = 34
  Placement = pos=(-17,-36.25,26) rot=(0,0,1;0rad)
  Width = 8
FEATURE [Part::Box] Box097  label="Krychle097"
  AttacherType = Attacher::AttachEngine3D
  Height = 40
  Length = 56.5
  Placement = pos=(-28.25,-28.25,34) rot=(0,0,1;0rad)
  Width = 56.5
FEATURE [Part::Box] Box098  label="Krychle098"
  AttacherType = Attacher::AttachEngine3D
  Height = 8
  Length = 64
  Placement = pos=(-32,-32,26) rot=(0,0,1;0rad)
  Width = 64
FEATURE [Part::Cylinder] Cylinder225  label="Válec225"
  Angle = 360
  AttacherType = Attacher::AttachEngine3D
  Height = 20
  Placement = pos=(0,0,15) rot=(0,0,1;0rad)
  Radius = 12
FEATURE [Part::Cylinder] Cylinder226  label="Válec226"
  Angle = 360
  AttacherType = Attacher::AttachEngine3D
  Height = 3
  Placement = pos=(2e-15,16,2) rot=(0,0,-1;1.1781rad)
  Radius = 3
FEATURE [Part::Cylinder] Cylinder227  label="Válec227"
  Angle = 360
  AttacherType = Attacher::AttachEngine3D
  Height = 3
  Placement = pos=(-1.2e-14,-16,2) rot=(0,0,1;1.96349rad)
  Radius = 3
FEATURE [Part::Cylinder] Cylinder228  label="Válec228"
  Angle = 360
  AttacherType = Attacher::AttachEngine3D
  Height = 3
  Placement = pos=(-16,7e-15,2) rot=(0,0,1;0.392699rad)
  Radius = 3
FEATURE [Part::Cylinder] Cylinder229  label="Válec229"
  Angle = 360
  AttacherType = Attacher::AttachEngine3D
  Height = 3
  Placement = pos=(16,0,2) rot=(0,0,1;3.53429rad)
  Radius = 3
FEATURE [Part::Compound] Compound248
  Links = -> [Cylinder227,Cylinder228,Cylinder226,Cylinder229]
  Placement = pos=(0,0,29) rot=(0,0,1;0.785398rad)
FEATURE [Part::Cylinder] Cylinder230  label="Válec230"
  Angle = 360
  AttacherType = Attacher::AttachEngine3D
  Height = 12
  Placement = pos=(0,-32.55,100) rot=(0,1,0;1.5708rad)
  Radius = 5
FEATURE [Part::Compound] Compound247
  Links = -> [Cylinder224,Cylinder230]
FEATURE [Part::Cylinder] Cylinder231  label="Válec231"
  Angle = 360
  AttacherType = Attacher::AttachEngine3D
  Height = 50
  Placement = pos=(0,100,66) rot=(0,1,0;1.5708rad)
  Radius = 2.5
FEATURE [Part::Compound] Compound249
  Links = -> [Cylinder231]
  Placement = pos=(0,0,100) rot=(0,0,1;0rad)
FEATURE [Part::Cut] Cut103
  Base = -> Box096
  Tool = -> Compound249
FEATURE [Part::Box] Box099  label="Krychle099"
  AttacherType = Attacher::AttachEngine3D
  Height = 58
  Length = 20
  Placement = pos=(-10,-46.25,26) rot=(0,0,1;0rad)
  Width = 10
FEATURE [Part::Cut] Cut110
  Base = -> Cut103
  Tool = -> Compound247
FEATURE [Part::Cylinder] Cylinder232  label="Válec232"
  Angle = 360
  AttacherType = Attacher::AttachEngine3D
  Height = 20
  Placement = pos=(23.55,-23.55,20) rot=(0,0,1;0rad)
  Radius = 2.5
FEATURE [Part::Cylinder] Cylinder233  label="Válec233"
  Angle = 360
  AttacherType = Attacher::AttachEngine3D
  Height = 4
  Placement = pos=(-23.55,-23.55,26) rot=(0,0,1;0rad)
  Radius = 5
FEATURE [Part::Cylinder] Cylinder234  label="Válec234"
  Angle = 360
  AttacherType = Attacher::AttachEngine3D
  Height = 4
  Placement = pos=(23.55,-23.55,26) rot=(0,0,1;0rad)
  Radius = 5
FEATURE [Part::Cylinder] Cylinder235  label="Válec235"
  Angle = 360
  AttacherType = Attacher::AttachEngine3D
  Height = 30
  Placement = pos=(-1.2e-14,-16,2) rot=(0,0,1;1.96349rad)
  Radius = 1.5
FEATURE [Part::Cylinder] Cylinder236  label="Válec236"
  Angle = 360
  AttacherType = Attacher::AttachEngine3D
  Height = 30
  Placement = pos=(2e-15,16,2) rot=(0,0,-1;1.1781rad)
  Radius = 1.5
FEATURE [Part::Cylinder] Cylinder237  label="Válec237"
  Angle = 360
  AttacherType = Attacher::AttachEngine3D
  Height = 30
  Placement = pos=(-16,7e-15,2) rot=(0,0,1;0.392699rad)
  Radius = 1.5
FEATURE [Part::Cylinder] Cylinder238  label="Válec238"
  Angle = 360
  AttacherType = Attacher::AttachEngine3D
  Height = 4
  Placement = pos=(23.55,23.55,26) rot=(0,0,1;0rad)
  Radius = 5
FEATURE [Part::Cylinder] Cylinder239  label="Válec239"
  Angle = 360
  AttacherType = Attacher::AttachEngine3D
  Height = 20
  Placement = pos=(23.55,23.55,20) rot=(0,0,1;0rad)
  Radius = 2.5
FEATURE [Part::Cylinder] Cylinder240  label="Válec240"
  Angle = 360
  AttacherType = Attacher::AttachEngine3D
  Height = 20
  Placement = pos=(-23.55,-23.55,20) rot=(0,0,1;0rad)
  Radius = 2.5
FEATURE [Part::Cylinder] Cylinder241  label="Válec241"
  Angle = 360
  AttacherType = Attacher::AttachEngine3D
  Height = 30
  Placement = pos=(16,0,2) rot=(0,0,1;3.53429rad)
  Radius = 1.5
FEATURE [Part::Compound] Compound252
  Links = -> [Cylinder235,Cylinder237,Cylinder236,Cylinder241]
  Placement = pos=(0,0,14) rot=(0,0,1;0.785398rad)
FEATURE [Part::Cut] Cut107
  Base = -> Box098
  Tool = -> Compound252
FEATURE [Part::Cut] Cut109
  Base = -> Cut107
  Tool = -> Compound248
FEATURE [Part::Cylinder] Cylinder242  label="Válec242"
  Angle = 360
  AttacherType = Attacher::AttachEngine3D
  Height = 4
  Placement = pos=(-23.55,23.55,26) rot=(0,0,1;0rad)
  Radius = 5
FEATURE [Part::Compound] Compound250
  Links = -> [Cylinder233,Cylinder238,Cylinder234,Cylinder242]
FEATURE [Part::Box] Box100  label="Krychle100"
  AttacherType = Attacher::AttachEngine3D
  Height = 16
  Length = 64
  Placement = pos=(-32,-32,34) rot=(0,0,1;0rad)
  Width = 64
FEATURE [Part::Cut] Cut108
  Base = -> Box100
  Tool = -> Box097
FEATURE [Part::Cylinder] Cylinder243  label="Válec243"
  Angle = 360
  AttacherType = Attacher::AttachEngine3D
  Height = 20
  Placement = pos=(-23.55,23.55,20) rot=(0,0,1;0rad)
  Radius = 2.5
FEATURE [Part::Compound] Compound253
  Links = -> [Cylinder239,Cylinder243,Cylinder240,Cylinder232]
FEATURE [Part::Cut] Cut106
  Base = -> Cut109
  Tool = -> Compound253
FEATURE [Part::Cut] Cut102
  Base = -> Cut106
  Tool = -> Compound250
FEATURE [Part::Cut] Cut104
  Base = -> Cut102
  Tool = -> Cylinder225
FEATURE [Part::Compound] Compound246  label="hrubo_holder004"
  Links = -> [Cut104,Cut110,Cut108]
FEATURE [Part::Box] Box101  label="Krychle101"
  AttacherType = Attacher::AttachEngine3D
  Height = 42
  Length = 34
  Placement = pos=(36.25,-17,26) rot=(0,0,1;1.5708rad)
  Width = 8
FEATURE [Part::Box] Box102  label="Krychle102"
  AttacherType = Attacher::AttachEngine3D
  Height = 42
  Length = 34
  Placement = pos=(-36.25,17,26) rot=(0,0,-1;1.5708rad)
  Width = 8
FEATURE [Part::Compound] Compound258  label="hrubo_holder006"
  Links = -> [Box099,Compound246]
FEATURE [Part::Box] Box103  label="Krychle103"
  AttacherType = Attacher::AttachEngine3D
  Height = 9
  Length = 10
  Placement = pos=(-10,-10,63) rot=(0,0,1;0rad)
  Width = 48
FEATURE [Part::Box] Box104  label="Krychle104"
  AttacherType = Attacher::AttachEngine3D
  Height = 9
  Length = 14.62
  Placement = pos=(-58,38,63) rot=(0,0,1;0rad)
  Width = 10
FEATURE [Part::Box] Box105  label="Krychle105"
  AttacherType = Attacher::AttachEngine3D
  Height = 20
  Length = 28.77
  Placement = pos=(-14.38,-8,34) rot=(0,0,1;0rad)
  Width = 43.38
FEATURE [Part::Cut] Cut105
  Base = -> Compound258
  Placement = pos=(-29,18,30) rot=(0,0,1;0rad)
  Tool = -> Box105
FEATURE [Part::Compound] Compound251
  Links = -> [Cut105]
  Placement = pos=(29,-18,-30) rot=(0,0,1;0rad)
FEATURE [Part::Box] Box106  label="Krychle106"
  AttacherType = Attacher::AttachEngine3D
  Height = 9
  Length = 38
  Placement = pos=(-48,-10,63) rot=(0,0,1;0rad)
  Width = 10
FEATURE [Part::Box] Box107  label="Krychle107"
  AttacherType = Attacher::AttachEngine3D
  Height = 9
  Length = 14.62
  Placement = pos=(-14.615,38,63) rot=(0,0,1;0rad)
  Width = 10
FEATURE [Part::Cylinder] Cylinder244  label="Válec244"
  Angle = 360
  AttacherType = Attacher::AttachEngine3D
  Height = 50
  Placement = pos=(23.55,23.55,20) rot=(0,0,1;0rad)
  Radius = 2.5
FEATURE [Part::Box] Box108  label="Krychle108"
  AttacherType = Attacher::AttachEngine3D
  Height = 9
  Length = 10
  Placement = pos=(-58,-10,63) rot=(0,0,1;0rad)
  Width = 48
FEATURE [Part::Compound] Compound255
  Links = -> [Box104,Box103,Box108,Box107,Box106]
  Placement = pos=(29,-19,-4) rot=(0,0,1;0rad)
FEATURE [Part::Cylinder] Cylinder245  label="Válec245"
  Angle = 360
  AttacherType = Attacher::AttachEngine3D
  Height = 50
  Placement = pos=(-23.55,23.55,20) rot=(0,0,1;0rad)
  Radius = 2.5
FEATURE [Part::Cylinder] Cylinder246  label="Válec246"
  Angle = 360
  AttacherType = Attacher::AttachEngine3D
  Height = 50
  Placement = pos=(-23.55,-23.55,20) rot=(0,0,1;0rad)
  Radius = 2.5
FEATURE [Part::Cylinder] Cylinder247  label="Válec247"
  Angle = 360
  AttacherType = Attacher::AttachEngine3D
  Height = 50
  Placement = pos=(23.55,-23.55,20) rot=(0,0,1;0rad)
  Radius = 2.5
FEATURE [Part::Compound] Compound256
  Links = -> [Cylinder244,Cylinder247,Cylinder246,Cylinder245]
FEATURE [Part::Cut] Cut101
  Base = -> Compound255
  Placement = pos=(0,0,-25) rot=(0,0,1;0rad)
  Tool = -> Compound256
FEATURE [Part::Compound] Compound254  label="hrubo_holder_nuovo001"
  Links = -> [Compound251,Cut101]
FEATURE [Part::Box] Box109  label="Krychle109"
  AttacherType = Attacher::AttachEngine3D
  Height = 6
  Length = 8
  Placement = pos=(3,-48,34) rot=(0,0,1;0rad)
  Width = 2
FEATURE [Part::Box] Box110  label="Krychle110"
  AttacherType = Attacher::AttachEngine3D
  Height = 6
  Length = 8
  Placement = pos=(-11,-48,34) rot=(0,0,1;0rad)
  Width = 2
FEATURE [Part::Box] Box111  label="Krychle111"
  AttacherType = Attacher::AttachEngine3D
  Height = 6
  Length = 8
  Placement = pos=(3,-48,70) rot=(0,0,1;0rad)
  Width = 2
FEATURE [Part::Box] Box112  label="Krychle112"
  AttacherType = Attacher::AttachEngine3D
  Height = 6
  Length = 8
  Placement = pos=(-11,-48,70) rot=(0,0,1;0rad)
  Width = 2
FEATURE [Part::Cylinder] Cylinder248  label="Válec248"
  Angle = 360
  AttacherType = Attacher::AttachEngine3D
  Height = 20
  Placement = pos=(7,-34,37) rot=(1,0,0;1.5708rad)
  Radius = 1.5
FEATURE [Part::Cylinder] Cylinder249  label="Válec249"
  Angle = 360
  AttacherType = Attacher::AttachEngine3D
  Height = 20
  Placement = pos=(-7,-34,37) rot=(1,0,0;1.5708rad)
  Radius = 1.5
FEATURE [Part::Cylinder] Cylinder250  label="Válec250"
  Angle = 360
  AttacherType = Attacher::AttachEngine3D
  Height = 20
  Placement = pos=(7,-34,73) rot=(1,0,0;1.5708rad)
  Radius = 1.5
FEATURE [Part::Cylinder] Cylinder251  label="Válec251"
  Angle = 360
  AttacherType = Attacher::AttachEngine3D
  Height = 20
  Placement = pos=(-7,-34,73) rot=(1,0,0;1.5708rad)
  Radius = 1.5
FEATURE [Part::Compound] Compound259
  Links = -> [Cylinder248,Cylinder249,Cylinder250,Cylinder251]
FEATURE [Part::Compound] Compound257  label="hrubo_holder005"
  Links = -> [Box101,Box102,Cut101,Compound254]
FEATURE [Part::Cut] Cut111
  Base = -> Compound245
  Tool = -> Compound259
FEATURE [Part::Compound] Compound260
  Links = -> [Box109,Box110,Box111,Box112]
  Placement = pos=(0,9.75,0) rot=(0,0,1;0rad)
FEATURE [Part::Cut] Cut112  label="htubo_motor_holder"
  Base = -> Cut111
  Tool = -> Compound260
FEATURE [Part::Cylinder] Cylinder252  label="Válec252"
  Angle = 360
  AttacherType = Attacher::AttachEngine3D
  Height = 12
  Placement = pos=(0,-32.55,100) rot=(0.57735,-0.57735,-0.57735;4.18879rad)
  Radius = 5
FEATURE [Part::Box] Box113  label="Krychle113"
  AttacherType = Attacher::AttachEngine3D
  Height = 58
  Length = 34
  Placement = pos=(-17,-36.25,26) rot=(0,0,1;0rad)
  Width = 8
FEATURE [Part::Box] Box114  label="Krychle114"
  AttacherType = Attacher::AttachEngine3D
  Height = 40
  Length = 56.5
  Placement = pos=(-28.25,-28.25,34) rot=(0,0,1;0rad)
  Width = 56.5
FEATURE [Part::Box] Box115  label="Krychle115"
  AttacherType = Attacher::AttachEngine3D
  Height = 8
  Length = 64
  Placement = pos=(-32,-32,26) rot=(0,0,1;0rad)
  Width = 64
FEATURE [Part::Cylinder] Cylinder253  label="Válec253"
  Angle = 360
  AttacherType = Attacher::AttachEngine3D
  Height = 20
  Placement = pos=(0,0,15) rot=(0,0,1;0rad)
  Radius = 12
FEATURE [Part::Cylinder] Cylinder254  label="Válec254"
  Angle = 360
  AttacherType = Attacher::AttachEngine3D
  Height = 3
  Placement = pos=(2e-15,16,2) rot=(0,0,-1;1.1781rad)
  Radius = 3
FEATURE [Part::Cylinder] Cylinder255  label="Válec255"
  Angle = 360
  AttacherType = Attacher::AttachEngine3D
  Height = 3
  Placement = pos=(-1.2e-14,-16,2) rot=(0,0,1;1.96349rad)
  Radius = 3
FEATURE [Part::Cylinder] Cylinder256  label="Válec256"
  Angle = 360
  AttacherType = Attacher::AttachEngine3D
  Height = 3
  Placement = pos=(-16,7e-15,2) rot=(0,0,1;0.392699rad)
  Radius = 3
FEATURE [Part::Cylinder] Cylinder257  label="Válec257"
  Angle = 360
  AttacherType = Attacher::AttachEngine3D
  Height = 3
  Placement = pos=(16,0,2) rot=(0,0,1;3.53429rad)
  Radius = 3
FEATURE [Part::Compound] Compound264
  Links = -> [Cylinder255,Cylinder256,Cylinder254,Cylinder257]
  Placement = pos=(0,0,29) rot=(0,0,1;0.785398rad)
FEATURE [Part::Cylinder] Cylinder258  label="Válec258"
  Angle = 360
  AttacherType = Attacher::AttachEngine3D
  Height = 12
  Placement = pos=(0,-32.55,100) rot=(0,1,0;1.5708rad)
  Radius = 5
FEATURE [Part::Compound] Compound263
  Links = -> [Cylinder252,Cylinder258]
FEATURE [Part::Cylinder] Cylinder259  label="Válec259"
  Angle = 360
  AttacherType = Attacher::AttachEngine3D
  Height = 50
  Placement = pos=(0,100,66) rot=(0,1,0;1.5708rad)
  Radius = 2.5
FEATURE [Part::Compound] Compound265
  Links = -> [Cylinder259]
  Placement = pos=(0,0,100) rot=(0,0,1;0rad)
FEATURE [Part::Cut] Cut115
  Base = -> Box113
  Tool = -> Compound265
FEATURE [Part::Box] Box116  label="Krychle116"
  AttacherType = Attacher::AttachEngine3D
  Height = 58
  Length = 20
  Placement = pos=(-10,-46.25,26) rot=(0,0,1;0rad)
  Width = 10
FEATURE [Part::Cut] Cut124
  Base = -> Cut115
  Tool = -> Compound263
FEATURE [Part::Cylinder] Cylinder260  label="Válec260"
  Angle = 360
  AttacherType = Attacher::AttachEngine3D
  Height = 20
  Placement = pos=(23.55,-23.55,20) rot=(0,0,1;0rad)
  Radius = 2.5
FEATURE [Part::Cylinder] Cylinder261  label="Válec261"
  Angle = 360
  AttacherType = Attacher::AttachEngine3D
  Height = 4
  Placement = pos=(-23.55,-23.55,26) rot=(0,0,1;0rad)
  Radius = 5
FEATURE [Part::Cylinder] Cylinder262  label="Válec262"
  Angle = 360
  AttacherType = Attacher::AttachEngine3D
  Height = 4
  Placement = pos=(23.55,-23.55,26) rot=(0,0,1;0rad)
  Radius = 5
FEATURE [Part::Cylinder] Cylinder263  label="Válec263"
  Angle = 360
  AttacherType = Attacher::AttachEngine3D
  Height = 30
  Placement = pos=(-1.2e-14,-16,2) rot=(0,0,1;1.96349rad)
  Radius = 1.5
FEATURE [Part::Cylinder] Cylinder264  label="Válec264"
  Angle = 360
  AttacherType = Attacher::AttachEngine3D
  Height = 30
  Placement = pos=(2e-15,16,2) rot=(0,0,-1;1.1781rad)
  Radius = 1.5
FEATURE [Part::Cylinder] Cylinder265  label="Válec265"
  Angle = 360
  AttacherType = Attacher::AttachEngine3D
  Height = 30
  Placement = pos=(-16,7e-15,2) rot=(0,0,1;0.392699rad)
  Radius = 1.5
FEATURE [Part::Cylinder] Cylinder266  label="Válec266"
  Angle = 360
  AttacherType = Attacher::AttachEngine3D
  Height = 4
  Placement = pos=(23.55,23.55,26) rot=(0,0,1;0rad)
  Radius = 5
FEATURE [Part::Cylinder] Cylinder267  label="Válec267"
  Angle = 360
  AttacherType = Attacher::AttachEngine3D
  Height = 20
  Placement = pos=(23.55,23.55,20) rot=(0,0,1;0rad)
  Radius = 2.5
FEATURE [Part::Cylinder] Cylinder268  label="Válec268"
  Angle = 360
  AttacherType = Attacher::AttachEngine3D
  Height = 20
  Placement = pos=(-23.55,-23.55,20) rot=(0,0,1;0rad)
  Radius = 2.5
FEATURE [Part::Cylinder] Cylinder269  label="Válec269"
  Angle = 360
  AttacherType = Attacher::AttachEngine3D
  Height = 30
  Placement = pos=(16,0,2) rot=(0,0,1;3.53429rad)
  Radius = 1.5
FEATURE [Part::Compound] Compound268
  Links = -> [Cylinder263,Cylinder265,Cylinder264,Cylinder269]
  Placement = pos=(0,0,14) rot=(0,0,1;0.785398rad)
FEATURE [Part::Cut] Cut121
  Base = -> Box115
  Tool = -> Compound268
FEATURE [Part::Cut] Cut123
  Base = -> Cut121
  Tool = -> Compound264
FEATURE [Part::Cylinder] Cylinder270  label="Válec270"
  Angle = 360
  AttacherType = Attacher::AttachEngine3D
  Height = 4
  Placement = pos=(-23.55,23.55,26) rot=(0,0,1;0rad)
  Radius = 5
FEATURE [Part::Compound] Compound266
  Links = -> [Cylinder261,Cylinder266,Cylinder262,Cylinder270]
  Placement = pos=(0,0,-50) rot=(0,0,1;0rad)
FEATURE [Part::Box] Box117  label="Krychle117"
  AttacherType = Attacher::AttachEngine3D
  Height = 16
  Length = 64
  Placement = pos=(-32,-32,34) rot=(0,0,1;0rad)
  Width = 64
FEATURE [Part::Cut] Cut122
  Base = -> Box117
  Tool = -> Box114
FEATURE [Part::Cylinder] Cylinder271  label="Válec271"
  Angle = 360
  AttacherType = Attacher::AttachEngine3D
  Height = 20
  Placement = pos=(-23.55,23.55,20) rot=(0,0,1;0rad)
  Radius = 2.5
FEATURE [Part::Compound] Compound269
  Links = -> [Cylinder267,Cylinder271,Cylinder268,Cylinder260]
FEATURE [Part::Cut] Cut120
  Base = -> Cut123
  Tool = -> Compound269
FEATURE [Part::Cut] Cut114
  Base = -> Cut120
  Tool = -> Compound266
FEATURE [Part::Cut] Cut116
  Base = -> Cut114
  Tool = -> Cylinder253
FEATURE [Part::Compound] Compound261  label="hrubo_holder007"
  Links = -> [Cut116,Cut124,Cut122]
FEATURE [Part::Box] Box120  label="Krychle120"
  AttacherType = Attacher::AttachEngine3D
  Height = 6
  Length = 8
  Placement = pos=(-11,-48,34) rot=(0,0,1;0rad)
  Width = 2
FEATURE [Part::Cylinder] Cylinder272  label="Válec272"
  Angle = 360
  AttacherType = Attacher::AttachEngine3D
  Height = 20
  Placement = pos=(-7,-34,37) rot=(1,0,0;1.5708rad)
  Radius = 1.5
FEATURE [Part::Box] Box121  label="Krychle121"
  AttacherType = Attacher::AttachEngine3D
  Height = 6
  Length = 8
  Placement = pos=(3,-48,34) rot=(0,0,1;0rad)
  Width = 2
FEATURE [Part::Box] Box122  label="Krychle122"
  AttacherType = Attacher::AttachEngine3D
  Height = 6
  Length = 8
  Placement = pos=(3,-48,70) rot=(0,0,1;0rad)
  Width = 2
FEATURE [Part::Box] Box123  label="Krychle123"
  AttacherType = Attacher::AttachEngine3D
  Height = 6
  Length = 8
  Placement = pos=(-11,-48,70) rot=(0,0,1;0rad)
  Width = 2
FEATURE [Part::Compound] Compound262
  Links = -> [Box121,Box120,Box122,Box123]
  Placement = pos=(0,9.75,0) rot=(0,0,1;0rad)
FEATURE [Part::Cylinder] Cylinder273  label="Válec273"
  Angle = 360
  AttacherType = Attacher::AttachEngine3D
  Height = 20
  Placement = pos=(7,-34,37) rot=(1,0,0;1.5708rad)
  Radius = 1.5
FEATURE [Part::Cylinder] Cylinder274  label="Válec274"
  Angle = 360
  AttacherType = Attacher::AttachEngine3D
  Height = 20
  Placement = pos=(7,-34,73) rot=(1,0,0;1.5708rad)
  Radius = 1.5
FEATURE [Part::Cylinder] Cylinder275  label="Válec275"
  Angle = 360
  AttacherType = Attacher::AttachEngine3D
  Height = 20
  Placement = pos=(-7,-34,73) rot=(1,0,0;1.5708rad)
  Radius = 1.5
FEATURE [Part::Compound] Compound273
  Links = -> [Cylinder273,Cylinder272,Cylinder274,Cylinder275]
FEATURE [Part::Compound] Compound275  label="hrubo_holder009"
  Links = -> [Box116,Compound261]
FEATURE [Part::Box] Box126  label="Krychle126"
  AttacherType = Attacher::AttachEngine3D
  Height = 20
  Length = 28.8
  Placement = pos=(-14.4,-8,34) rot=(0,0,1;0rad)
  Width = 43.38
FEATURE [Part::Cut] Cut117
  Base = -> Compound275
  Placement = pos=(-29,18,30) rot=(0,0,1;0rad)
  Tool = -> Box126
FEATURE [Part::Compound] Compound267
  Links = -> [Cut117]
  Placement = pos=(29,-18,-30) rot=(0,0,1;0rad)
FEATURE [Part::Compound] Compound270  label="hrubo_holder_nuovo002"
  Links = -> [Compound267]
FEATURE [Part::Box] Box130  label="Krychle130"
  AttacherType = Attacher::AttachEngine3D
  Height = 9
  Length = 10
  Placement = pos=(-58,-10,63) rot=(0,0,1;0rad)
  Width = 48
FEATURE [Part::Box] Box131  label="Krychle131"
  AttacherType = Attacher::AttachEngine3D
  Height = 9
  Length = 14.6
  Placement = pos=(-58,38,63) rot=(0,0,1;0rad)
  Width = 10
FEATURE [Part::Cylinder] Cylinder280  label="Válec280"
  Angle = 360
  AttacherType = Attacher::AttachEngine3D
  Height = 50
  Placement = pos=(-23.55,-23.55,20) rot=(0,0,1;0rad)
  Radius = 2.5
FEATURE [Part::Box] Box132  label="Krychle132"
  AttacherType = Attacher::AttachEngine3D
  Height = 9
  Length = 38
  Placement = pos=(-48,-10,63) rot=(0,0,1;0rad)
  Width = 10
FEATURE [Part::Cylinder] Cylinder281  label="Válec281"
  Angle = 360
  AttacherType = Attacher::AttachEngine3D
  Height = 50
  Placement = pos=(23.55,23.55,20) rot=(0,0,1;0rad)
  Radius = 2.5
FEATURE [Part::Box] Box133  label="Krychle133"
  AttacherType = Attacher::AttachEngine3D
  Height = 9
  Length = 14.62
  Placement = pos=(-14.6,38,63) rot=(0,0,1;0rad)
  Width = 10
FEATURE [Part::Cylinder] Cylinder282  label="Válec282"
  Angle = 360
  AttacherType = Attacher::AttachEngine3D
  Height = 50
  Placement = pos=(-23.55,23.55,20) rot=(0,0,1;0rad)
  Radius = 2.5
FEATURE [Part::Box] Box134  label="Krychle134"
  AttacherType = Attacher::AttachEngine3D
  Height = 9
  Length = 10
  Placement = pos=(-10,-10,63) rot=(0,0,1;0rad)
  Width = 48
FEATURE [Part::Compound] Compound277
  Links = -> [Box131,Box134,Box130,Box133,Box132]
  Placement = pos=(29,-19,-4) rot=(0,0,1;0rad)
FEATURE [Part::Cylinder] Cylinder283  label="Válec283"
  Angle = 360
  AttacherType = Attacher::AttachEngine3D
  Height = 50
  Placement = pos=(23.55,-23.55,20) rot=(0,0,1;0rad)
  Radius = 2.5
FEATURE [Part::Compound] Compound276
  Links = -> [Cylinder281,Cylinder283,Cylinder280,Cylinder282]
FEATURE [Part::Cut] Cut125
  Base = -> Compound277
  Placement = pos=(0,0,-25) rot=(0,0,1;0rad)
  Tool = -> Compound276
FEATURE [Part::Chamfer] Chamfer031
  Base = -> Cut125
  Edges = 1 edges r=2: [Edge46]
FEATURE [Part::Chamfer] Chamfer032  label="podlo_AMT"
  Base = -> Chamfer031
  Edges = 1 edges r=2: [Edge24]
FEATURE [Part::Box] Box118  label="Krychle118"
  AttacherType = Attacher::AttachEngine3D
  Height = 42
  Length = 34
  Placement = pos=(36.25,100,36) rot=(0,0,1;1.5708rad)
  Width = 8
FEATURE [Part::Box] Box119  label="Krychle119"
  AttacherType = Attacher::AttachEngine3D
  Height = 42
  Length = 34
  Placement = pos=(-36.25,100,26) rot=(0,0,-1;1.5708rad)
  Width = 8
FEATURE [Part::Compound] Compound274  label="hrubo_holder008"
  Links = -> [Box118,Box119,Compound270]
FEATURE [Part::Cut] Cut118
  Base = -> Compound274
  Tool = -> Compound273
FEATURE [Part::Cut] Cut119  label="motor_holder"
  Base = -> Cut118
  Tool = -> Compound262
FEATURE [Part::Fillet] Fillet
  Base = -> Cut119
  Edges = 2 edges r=8: [Edge25,Edge38]
FEATURE [Part::Chamfer] Chamfer024
  Base = -> Fillet
  Edges = 2 edges r=3: [Edge175,Edge200]
FEATURE [Part::Chamfer] Chamfer025
  Base = -> Chamfer024
  Edges = 2 edges r=3: [Edge1,Edge5]
FEATURE [Part::Chamfer] Chamfer026
  Base = -> Chamfer025
  Edges = 4 edges r=3: [Edge149,Edge154,Edge222,Edge227]
FEATURE [Part::Chamfer] Chamfer027
  Base = -> Chamfer026
  Edges = 4 edges r=3: [Edge4,Edge28,Edge83,Edge111]
FEATURE [Part::Chamfer] Chamfer028
  Base = -> Chamfer027
  Edges = 4 edges r=3: [Edge257,Edge261,Edge269,Edge273]
FEATURE [Part::Chamfer] Chamfer029
  Base = -> Chamfer028
  Edges = 2 edges r=3: [Edge19,Edge23]
FEATURE [Part::Chamfer] Chamfer030  label="motor_holdo_noAMT"
  Base = -> Chamfer029
  Edges = 2 edges r=3: [Edge23,Edge27]
FEATURE [Part::Chamfer] Chamfer033
  Base = -> Chamfer030
  Edges = 2 edges r=2: [Edge130,Edge134]
FEATURE [Part::Chamfer] Chamfer034
  Base = -> Chamfer033
  Edges = 1 edges r=2: [Edge37]
FEATURE [Part::Chamfer] Chamfer035  label="moto_holder_noAMT"
  Base = -> Chamfer034
  Edges = 2 edges r=2: [Edge33,Edge41]
FEATURE [Part::Compound] Compound278  label="moto_holder_AMT"
  Links = -> [Chamfer035,Chamfer032]
FEATURE [Part::Box] Box136  label="Krychle136"
  AttacherType = Attacher::AttachEngine3D
  Height = 40
  Length = 56.5
  Placement = pos=(-28.25,-28.25,34) rot=(0,0,1;0rad)
  Width = 56.5
FEATURE [Part::Box] Box137  label="Krychle137"
  AttacherType = Attacher::AttachEngine3D
  Height = 58
  Length = 20
  Placement = pos=(-10,-46.25,26) rot=(0,0,1;0rad)
  Width = 10
FEATURE [Part::Cylinder] Cylinder288  label="Válec288"
  Angle = 360
  AttacherType = Attacher::AttachEngine3D
  Height = 12
  Placement = pos=(0,-32.55,100) rot=(0.57735,-0.57735,-0.57735;4.18879rad)
  Radius = 5
FEATURE [Part::Box] Box138  label="Krychle138"
  AttacherType = Attacher::AttachEngine3D
  Height = 58
  Length = 34
  Placement = pos=(-17,-36.25,26) rot=(0,0,1;0rad)
  Width = 8
FEATURE [Part::Cylinder] Cylinder292  label="Válec292"
  Angle = 360
  AttacherType = Attacher::AttachEngine3D
  Height = 12
  Placement = pos=(0,-32.55,100) rot=(0,1,0;1.5708rad)
  Radius = 5
FEATURE [Part::Compound] Compound289
  Links = -> [Cylinder288,Cylinder292]
FEATURE [Part::Cylinder] Cylinder293  label="Válec293"
  Angle = 360
  AttacherType = Attacher::AttachEngine3D
  Height = 50
  Placement = pos=(0,100,66) rot=(0,1,0;1.5708rad)
  Radius = 2.5
FEATURE [Part::Compound] Compound285
  Links = -> [Cylinder293]
  Placement = pos=(0,0,100) rot=(0,0,1;0rad)
FEATURE [Part::Cut] Cut126
  Base = -> Box138
  Tool = -> Compound285
FEATURE [Part::Cut] Cut135
  Base = -> Cut126
  Tool = -> Compound289
FEATURE [Part::Box] Box139  label="Krychle139"
  AttacherType = Attacher::AttachEngine3D
  Height = 6
  Length = 8
  Placement = pos=(3,-48,34) rot=(0,0,1;0rad)
  Width = 2
FEATURE [Part::Cylinder] Cylinder303  label="Válec303"
  Angle = 360
  AttacherType = Attacher::AttachEngine3D
  Height = 20
  Placement = pos=(7,-34,37) rot=(1,0,0;1.5708rad)
  Radius = 1.5
FEATURE [Part::Box] Box140  label="Krychle140"
  AttacherType = Attacher::AttachEngine3D
  Height = 6
  Length = 8
  Placement = pos=(-11,-48,70) rot=(0,0,1;0rad)
  Width = 2
FEATURE [Part::Box] Box141  label="Krychle141"
  AttacherType = Attacher::AttachEngine3D
  Height = 20
  Length = 28.8
  Placement = pos=(-14.4,-8,34) rot=(0,0,1;0rad)
  Width = 43.38
FEATURE [Part::Box] Box142  label="Krychle142"
  AttacherType = Attacher::AttachEngine3D
  Height = 16
  Length = 64
  Placement = pos=(-32,-32,34) rot=(0,0,1;0rad)
  Width = 64
FEATURE [Part::Cut] Cut130
  Base = -> Box142
  Tool = -> Box136
FEATURE [Part::Compound] Compound283  label="hrubo_holder010"
  Links = -> [Cut135,Cut130]
FEATURE [Part::Compound] Compound288  label="hrubo_holder011"
  Links = -> [Box137,Compound283]
FEATURE [Part::Cut] Cut131
  Base = -> Compound288
  Placement = pos=(-29,18,30) rot=(0,0,1;0rad)
  Tool = -> Box141
FEATURE [Part::Compound] Compound282
  Links = -> [Cut131]
  Placement = pos=(29,-18,-30) rot=(0,0,1;0rad)
FEATURE [Part::Compound] Compound287  label="hrubo_holder_nuovo003"
  Links = -> [Compound282]
FEATURE [Part::Compound] Compound291  label="hrubo_holder012"
  Links = -> [Compound287]
FEATURE [Part::Cylinder] Cylinder305  label="Válec305"
  Angle = 360
  AttacherType = Attacher::AttachEngine3D
  Height = 20
  Placement = pos=(-7,-34,73) rot=(1,0,0;1.5708rad)
  Radius = 1.5
FEATURE [Part::Box] Box143  label="Krychle143"
  AttacherType = Attacher::AttachEngine3D
  Height = 6
  Length = 8
  Placement = pos=(3,-48,70) rot=(0,0,1;0rad)
  Width = 2
FEATURE [Part::Cylinder] Cylinder306  label="Válec306"
  Angle = 360
  AttacherType = Attacher::AttachEngine3D
  Height = 20
  Placement = pos=(7,-34,73) rot=(1,0,0;1.5708rad)
  Radius = 1.5
FEATURE [Part::Cylinder] Cylinder307  label="Válec307"
  Angle = 360
  AttacherType = Attacher::AttachEngine3D
  Height = 20
  Placement = pos=(-7,-34,37) rot=(1,0,0;1.5708rad)
  Radius = 1.5
FEATURE [Part::Compound] Compound279
  Links = -> [Cylinder303,Cylinder307,Cylinder306,Cylinder305]
FEATURE [Part::Cut] Cut127
  Base = -> Compound291
  Tool = -> Compound279
FEATURE [Part::Box] Box144  label="Krychle144"
  AttacherType = Attacher::AttachEngine3D
  Height = 6
  Length = 8
  Placement = pos=(-11,-48,34) rot=(0,0,1;0rad)
  Width = 2
FEATURE [Part::Compound] Compound284
  Links = -> [Box139,Box144,Box143,Box140]
  Placement = pos=(0,9.75,0) rot=(0,0,1;0rad)
FEATURE [Part::Cut] Cut128  label="motor_holder001"
  Base = -> Cut127
  Tool = -> Compound284
FEATURE [Part::Box] Box145  label="Krychle145"
  AttacherType = Attacher::AttachEngine3D
  Height = 3
  Length = 16
  Placement = pos=(17.55,19.55,31) rot=(0,0,1;0rad)
  Width = 8
FEATURE [Part::Box] Box146  label="Krychle146"
  AttacherType = Attacher::AttachEngine3D
  Height = 3
  Length = 16
  Placement = pos=(17.55,-27.55,31) rot=(0,0,1;0rad)
  Width = 8
FEATURE [Part::Box] Box147  label="Krychle147"
  AttacherType = Attacher::AttachEngine3D
  Height = 3
  Length = 16
  Placement = pos=(-33.45,19.55,31) rot=(0,0,1;0rad)
  Width = 8
FEATURE [Part::Box] Box148  label="Krychle148"
  AttacherType = Attacher::AttachEngine3D
  Height = 3
  Length = 16
  Placement = pos=(-33.45,-27.55,31) rot=(0,0,1;0rad)
  Width = 8
FEATURE [Part::Compound] Compound292
  Links = -> [Box145,Box146,Box147,Box148]
FEATURE [Part::Cylinder] Cylinder308  label="Válec308"
  Angle = 360
  AttacherType = Attacher::AttachEngine3D
  Height = 4
  Placement = pos=(-23.55,-23.55,26) rot=(0,0,1;0rad)
  Radius = 5
FEATURE [Part::Cylinder] Cylinder309  label="Válec309"
  Angle = 360
  AttacherType = Attacher::AttachEngine3D
  Height = 3
  Placement = pos=(2e-15,16,2) rot=(0,0,-1;1.1781rad)
  Radius = 3
FEATURE [Part::Box] Box149  label="Krychle149"
  AttacherType = Attacher::AttachEngine3D
  Height = 8
  Length = 64
  Placement = pos=(-32,-32,26) rot=(0,0,1;0rad)
  Width = 64
FEATURE [Part::Cylinder] Cylinder310  label="Válec310"
  Angle = 360
  AttacherType = Attacher::AttachEngine3D
  Height = 20
  Placement = pos=(0,0,15) rot=(0,0,1;0rad)
  Radius = 12
FEATURE [Part::Cylinder] Cylinder311  label="Válec311"
  Angle = 360
  AttacherType = Attacher::AttachEngine3D
  Height = 4
  Placement = pos=(23.55,23.55,26) rot=(0,0,1;0rad)
  Radius = 5
FEATURE [Part::Cylinder] Cylinder312  label="Válec312"
  Angle = 360
  AttacherType = Attacher::AttachEngine3D
  Height = 20
  Placement = pos=(-23.55,-23.55,20) rot=(0,0,1;0rad)
  Radius = 2.5
FEATURE [Part::Cylinder] Cylinder313  label="Válec313"
  Angle = 360
  AttacherType = Attacher::AttachEngine3D
  Height = 30
  Placement = pos=(-16,7e-15,2) rot=(0,0,1;0.392699rad)
  Radius = 1.5
FEATURE [Part::Cylinder] Cylinder314  label="Válec314"
  Angle = 360
  AttacherType = Attacher::AttachEngine3D
  Height = 3
  Placement = pos=(-16,7e-15,2) rot=(0,0,1;0.392699rad)
  Radius = 3
FEATURE [Part::Cylinder] Cylinder315  label="Válec315"
  Angle = 360
  AttacherType = Attacher::AttachEngine3D
  Height = 4
  Placement = pos=(23.55,-23.55,26) rot=(0,0,1;0rad)
  Radius = 5
FEATURE [Part::Cylinder] Cylinder316  label="Válec316"
  Angle = 360
  AttacherType = Attacher::AttachEngine3D
  Height = 3
  Placement = pos=(16,0,2) rot=(0,0,1;3.53429rad)
  Radius = 3
FEATURE [Part::Cylinder] Cylinder317  label="Válec317"
  Angle = 360
  AttacherType = Attacher::AttachEngine3D
  Height = 30
  Placement = pos=(-1.2e-14,-16,2) rot=(0,0,1;1.96349rad)
  Radius = 1.5
FEATURE [Part::Cylinder] Cylinder318  label="Válec318"
  Angle = 360
  AttacherType = Attacher::AttachEngine3D
  Height = 3
  Placement = pos=(-1.2e-14,-16,2) rot=(0,0,1;1.96349rad)
  Radius = 3
FEATURE [Part::Compound] Compound293
  Links = -> [Cylinder318,Cylinder314,Cylinder309,Cylinder316]
  Placement = pos=(0,0,29) rot=(0,0,1;0.785398rad)
FEATURE [Part::Cylinder] Cylinder319  label="Válec319"
  Angle = 360
  AttacherType = Attacher::AttachEngine3D
  Height = 20
  Placement = pos=(23.55,-23.55,20) rot=(0,0,1;0rad)
  Radius = 2.5
FEATURE [Part::Cylinder] Cylinder320  label="Válec320"
  Angle = 360
  AttacherType = Attacher::AttachEngine3D
  Height = 30
  Placement = pos=(2e-15,16,2) rot=(0,0,-1;1.1781rad)
  Radius = 1.5
FEATURE [Part::Cylinder] Cylinder321  label="Válec321"
  Angle = 360
  AttacherType = Attacher::AttachEngine3D
  Height = 20
  Placement = pos=(23.55,23.55,20) rot=(0,0,1;0rad)
  Radius = 2.5
FEATURE [Part::Cylinder] Cylinder322  label="Válec322"
  Angle = 360
  AttacherType = Attacher::AttachEngine3D
  Height = 4
  Placement = pos=(-23.55,23.55,26) rot=(0,0,1;0rad)
  Radius = 5
FEATURE [Part::Compound] Compound296
  Links = -> [Cylinder308,Cylinder311,Cylinder315,Cylinder322]
  Placement = pos=(0,0,-50) rot=(0,0,1;0rad)
FEATURE [Part::Cylinder] Cylinder323  label="Válec323"
  Angle = 360
  AttacherType = Attacher::AttachEngine3D
  Height = 20
  Placement = pos=(-23.55,23.55,20) rot=(0,0,1;0rad)
  Radius = 2.5
FEATURE [Part::Compound] Compound295
  Links = -> [Cylinder321,Cylinder323,Cylinder312,Cylinder319]
FEATURE [Part::Cylinder] Cylinder324  label="Válec324"
  Angle = 360
  AttacherType = Attacher::AttachEngine3D
  Height = 30
  Placement = pos=(16,0,2) rot=(0,0,1;3.53429rad)
  Radius = 1.5
FEATURE [Part::Compound] Compound294
  Links = -> [Cylinder317,Cylinder313,Cylinder320,Cylinder324]
  Placement = pos=(0,0,14) rot=(0,0,1;0.785398rad)
FEATURE [Part::Cut] Cut137
  Base = -> Box149
  Tool = -> Compound294
FEATURE [Part::Cut] Cut140
  Base = -> Cut137
  Tool = -> Compound293
FEATURE [Part::Cut] Cut141
  Base = -> Cut140
  Tool = -> Compound295
FEATURE [Part::Cut] Cut138
  Base = -> Cut141
  Tool = -> Compound296
FEATURE [Part::Cut] Cut139
  Base = -> Cut138
  Tool = -> Cylinder310
FEATURE [Part::Cut] Cut142
  Base = -> Cut139
  Tool = -> Compound292
FEATURE [Part::Compound] Compound297  label="novo_moto_holder_hrubo"
  Links = -> [Cut128,Cut142]
FEATURE [Part::Cylinder] Cylinder325  label="Válec325"
  Angle = 360
  AttacherType = Attacher::AttachEngine3D
  Height = 50
  Placement = pos=(0,100,66) rot=(0,1,0;1.5708rad)
  Radius = 2.5
FEATURE [Part::Compound] Compound301
  Links = -> [Cylinder325]
  Placement = pos=(0,0,100) rot=(0,0,1;0rad)
FEATURE [Part::Box] Box150  label="Krychle150"
  AttacherType = Attacher::AttachEngine3D
  Height = 40
  Length = 56.5
  Placement = pos=(-28.25,-28.25,34) rot=(0,0,1;0rad)
  Width = 56.5
FEATURE [Part::Cylinder] Cylinder326  label="Válec326"
  Angle = 360
  AttacherType = Attacher::AttachEngine3D
  Height = 12
  Placement = pos=(0,-32.55,100) rot=(0.57735,-0.57735,-0.57735;4.18879rad)
  Radius = 5
FEATURE [Part::Box] Box151  label="Krychle151"
  AttacherType = Attacher::AttachEngine3D
  Height = 58
  Length = 34
  Placement = pos=(-17,-36.25,26) rot=(0,0,1;0rad)
  Width = 8
FEATURE [Part::Cut] Cut144
  Base = -> Box151
  Tool = -> Compound301
FEATURE [Part::Cylinder] Cylinder327  label="Válec327"
  Angle = 360
  AttacherType = Attacher::AttachEngine3D
  Height = 12
  Placement = pos=(0,-32.55,100) rot=(0,1,0;1.5708rad)
  Radius = 5
FEATURE [Part::Compound] Compound308
  Links = -> [Cylinder326,Cylinder327]
FEATURE [Part::Cut] Cut153
  Base = -> Cut144
  Tool = -> Compound308
FEATURE [Part::Box] Box152  label="Krychle152"
  AttacherType = Attacher::AttachEngine3D
  Height = 58
  Length = 20
  Placement = pos=(-10,-45.25,26) rot=(0,0,1;0rad)
  Width = 10
FEATURE [Part::Box] Box153  label="Krychle153"
  AttacherType = Attacher::AttachEngine3D
  Height = 6
  Length = 8
  Placement = pos=(3,-48,34) rot=(0,0,1;0rad)
  Width = 2
FEATURE [Part::Cylinder] Cylinder328  label="Válec328"
  Angle = 360
  AttacherType = Attacher::AttachEngine3D
  Height = 20
  Placement = pos=(-7,-34,73) rot=(1,0,0;1.5708rad)
  Radius = 1.5
FEATURE [Part::Box] Box154  label="Krychle154"
  AttacherType = Attacher::AttachEngine3D
  Height = 20
  Length = 28.8
  Placement = pos=(-14.4,-8,34) rot=(0,0,1;0rad)
  Width = 43.38
FEATURE [Part::Box] Box155  label="Krychle155"
  AttacherType = Attacher::AttachEngine3D
  Height = 16
  Length = 64
  Placement = pos=(-32,-32,34) rot=(0,0,1;0rad)
  Width = 64
FEATURE [Part::Cut] Cut151
  Base = -> Box155
  Tool = -> Box150
FEATURE [Part::Compound] Compound298  label="hrubo_holder013"
  Links = -> [Cut153,Cut151]
FEATURE [Part::Compound] Compound299  label="hrubo_holder014"
  Links = -> [Box152,Compound298]
FEATURE [Part::Cut] Cut150
  Base = -> Compound299
  Placement = pos=(-29,18,30) rot=(0,0,1;0rad)
  Tool = -> Box154
FEATURE [Part::Compound] Compound303
  Links = -> [Cut150]
  Placement = pos=(29,-18,-30) rot=(0,0,1;0rad)
FEATURE [Part::Compound] Compound305  label="hrubo_holder_nuovo004"
  Links = -> [Compound303]
FEATURE [Part::Compound] Compound306  label="hrubo_holder015"
  Links = -> [Compound305]
FEATURE [Part::Box] Box156  label="Krychle156"
  AttacherType = Attacher::AttachEngine3D
  Height = 6
  Length = 8
  Placement = pos=(3,-48,70) rot=(0,0,1;0rad)
  Width = 2
FEATURE [Part::Cylinder] Cylinder329  label="Válec329"
  Angle = 360
  AttacherType = Attacher::AttachEngine3D
  Height = 20
  Placement = pos=(7,-34,73) rot=(1,0,0;1.5708rad)
  Radius = 1.5
FEATURE [Part::Cylinder] Cylinder330  label="Válec330"
  Angle = 360
  AttacherType = Attacher::AttachEngine3D
  Height = 20
  Placement = pos=(-7,-34,37) rot=(1,0,0;1.5708rad)
  Radius = 1.5
FEATURE [Part::Box] Box157  label="Krychle157"
  AttacherType = Attacher::AttachEngine3D
  Height = 6
  Length = 8
  Placement = pos=(-11,-48,34) rot=(0,0,1;0rad)
  Width = 2
FEATURE [Part::Cylinder] Cylinder331  label="Válec331"
  Angle = 360
  AttacherType = Attacher::AttachEngine3D
  Height = 20
  Placement = pos=(7,-34,37) rot=(1,0,0;1.5708rad)
  Radius = 1.5
FEATURE [Part::Compound] Compound300
  Links = -> [Cylinder331,Cylinder330,Cylinder329,Cylinder328]
FEATURE [Part::Cut] Cut143
  Base = -> Compound306
  Tool = -> Compound300
FEATURE [Part::Box] Box158  label="Krychle158"
  AttacherType = Attacher::AttachEngine3D
  Height = 6
  Length = 8
  Placement = pos=(-11,-48,70) rot=(0,0,1;0rad)
  Width = 2
FEATURE [Part::Compound] Compound304
  Links = -> [Box153,Box157,Box156,Box158]
  Placement = pos=(0,9.75,0) rot=(0,0,1;0rad)
FEATURE [Part::Cut] Cut152  label="motor_holder002"
  Base = -> Cut143
  Tool = -> Compound304
FEATURE [Part::Cylinder] Cylinder332  label="Válec332"
  Angle = 360
  AttacherType = Attacher::AttachEngine3D
  Height = 3
  Placement = pos=(2e-15,16,2) rot=(0,0,-1;1.1781rad)
  Radius = 3
FEATURE [Part::Cylinder] Cylinder333  label="Válec333"
  Angle = 360
  AttacherType = Attacher::AttachEngine3D
  Height = 4
  Placement = pos=(-23.55,-23.55,26) rot=(0,0,1;0rad)
  Radius = 5
FEATURE [Part::Cylinder] Cylinder334  label="Válec334"
  Angle = 360
  AttacherType = Attacher::AttachEngine3D
  Height = 4
  Placement = pos=(23.55,-23.55,26) rot=(0,0,1;0rad)
  Radius = 5
FEATURE [Part::Box] Box159  label="Krychle159"
  AttacherType = Attacher::AttachEngine3D
  Height = 3
  Length = 16
  Placement = pos=(-33.45,19.55,31) rot=(0,0,1;0rad)
  Width = 8
FEATURE [Part::Box] Box160  label="Krychle160"
  AttacherType = Attacher::AttachEngine3D
  Height = 8
  Length = 64
  Placement = pos=(-32,-32,26) rot=(0,0,1;0rad)
  Width = 64
FEATURE [Part::Cylinder] Cylinder335  label="Válec335"
  Angle = 360
  AttacherType = Attacher::AttachEngine3D
  Height = 20
  Placement = pos=(0,0,15) rot=(0,0,1;0rad)
  Radius = 12
FEATURE [Part::Box] Box161  label="Krychle161"
  AttacherType = Attacher::AttachEngine3D
  Height = 3
  Length = 16
  Placement = pos=(-33.45,-27.55,31) rot=(0,0,1;0rad)
  Width = 8
FEATURE [Part::Cylinder] Cylinder336  label="Válec336"
  Angle = 360
  AttacherType = Attacher::AttachEngine3D
  Height = 3
  Placement = pos=(-16,7e-15,2) rot=(0,0,1;0.392699rad)
  Radius = 3
FEATURE [Part::Box] Box162  label="Krychle162"
  AttacherType = Attacher::AttachEngine3D
  Height = 3
  Length = 16
  Placement = pos=(17.55,-27.55,31) rot=(0,0,1;0rad)
  Width = 8
FEATURE [Part::Box] Box163  label="Krychle163"
  AttacherType = Attacher::AttachEngine3D
  Height = 3
  Length = 16
  Placement = pos=(17.55,19.55,31) rot=(0,0,1;0rad)
  Width = 8
FEATURE [Part::Cylinder] Cylinder337  label="Válec337"
  Angle = 360
  AttacherType = Attacher::AttachEngine3D
  Height = 4
  Placement = pos=(23.55,23.55,26) rot=(0,0,1;0rad)
  Radius = 5
FEATURE [Part::Cylinder] Cylinder338  label="Válec338"
  Angle = 360
  AttacherType = Attacher::AttachEngine3D
  Height = 20
  Placement = pos=(-23.55,-23.55,20) rot=(0,0,1;0rad)
  Radius = 2.5
FEATURE [Part::Cylinder] Cylinder339  label="Válec339"
  Angle = 360
  AttacherType = Attacher::AttachEngine3D
  Height = 30
  Placement = pos=(-16,7e-15,2) rot=(0,0,1;0.392699rad)
  Radius = 1.5
FEATURE [Part::Cylinder] Cylinder340  label="Válec340"
  Angle = 360
  AttacherType = Attacher::AttachEngine3D
  Height = 20
  Placement = pos=(23.55,-23.55,20) rot=(0,0,1;0rad)
  Radius = 2.5
FEATURE [Part::Cylinder] Cylinder341  label="Válec341"
  Angle = 360
  AttacherType = Attacher::AttachEngine3D
  Height = 30
  Placement = pos=(-1.2e-14,-16,2) rot=(0,0,1;1.96349rad)
  Radius = 1.5
FEATURE [Part::Cylinder] Cylinder342  label="Válec342"
  Angle = 360
  AttacherType = Attacher::AttachEngine3D
  Height = 3
  Placement = pos=(-1.2e-14,-16,2) rot=(0,0,1;1.96349rad)
  Radius = 3
FEATURE [Part::Cylinder] Cylinder343  label="Válec343"
  Angle = 360
  AttacherType = Attacher::AttachEngine3D
  Height = 3
  Placement = pos=(16,0,2) rot=(0,0,1;3.53429rad)
  Radius = 3
FEATURE [Part::Compound] Compound302
  Links = -> [Cylinder342,Cylinder336,Cylinder332,Cylinder343]
  Placement = pos=(0,0,29) rot=(0,0,1;0.785398rad)
FEATURE [Part::Cylinder] Cylinder344  label="Válec344"
  Angle = 360
  AttacherType = Attacher::AttachEngine3D
  Height = 20
  Placement = pos=(23.55,23.55,20) rot=(0,0,1;0rad)
  Radius = 2.5
FEATURE [Part::Cylinder] Cylinder345  label="Válec345"
  Angle = 360
  AttacherType = Attacher::AttachEngine3D
  Height = 4
  Placement = pos=(-23.55,23.55,26) rot=(0,0,1;0rad)
  Radius = 5
FEATURE [Part::Compound] Compound310
  Links = -> [Cylinder333,Cylinder337,Cylinder334,Cylinder345]
  Placement = pos=(0,0,-50) rot=(0,0,1;0rad)
FEATURE [Part::Cylinder] Cylinder346  label="Válec346"
  Angle = 360
  AttacherType = Attacher::AttachEngine3D
  Height = 30
  Placement = pos=(2e-15,16,2) rot=(0,0,-1;1.1781rad)
  Radius = 1.5
FEATURE [Part::Cylinder] Cylinder347  label="Válec347"
  Angle = 360
  AttacherType = Attacher::AttachEngine3D
  Height = 20
  Placement = pos=(-23.55,23.55,20) rot=(0,0,1;0rad)
  Radius = 2.5
FEATURE [Part::Compound] Compound309
  Links = -> [Cylinder344,Cylinder347,Cylinder338,Cylinder340]
FEATURE [Part::Cylinder] Cylinder348  label="Válec348"
  Angle = 360
  AttacherType = Attacher::AttachEngine3D
  Height = 30
  Placement = pos=(16,0,2) rot=(0,0,1;3.53429rad)
  Radius = 1.5
FEATURE [Part::Compound] Compound307
  Links = -> [Cylinder341,Cylinder339,Cylinder346,Cylinder348]
  Placement = pos=(0,0,14) rot=(0,0,1;0.785398rad)
FEATURE [Part::Cut] Cut148
  Base = -> Box160
  Tool = -> Compound307
FEATURE [Part::Cut] Cut145
  Base = -> Cut148
  Tool = -> Compound302
FEATURE [Part::Cut] Cut146
  Base = -> Cut145
  Tool = -> Compound309
FEATURE [Part::Cut] Cut149
  Base = -> Cut146
  Tool = -> Compound310
FEATURE [Part::Cut] Cut147
  Base = -> Cut149
  Tool = -> Cylinder335
FEATURE [Part::Compound] Compound311
  Links = -> [Box163,Box162,Box159,Box161]
FEATURE [Part::Cut] Cut154
  Base = -> Cut147
  Tool = -> Compound311
FEATURE [Part::Compound] Compound312  label="novo_moto_holder_hrubo001"
  Links = -> [Cut152,Cut154]
FEATURE [Part::Chamfer] Chamfer036
  Base = -> Compound312
  Edges = 4 edges r=2: [Edge109,Edge111,Edge154,Edge156]
FEATURE [Part::Chamfer] Chamfer037
  Base = -> Chamfer036
  Edges = 4 edges r=2: [Edge37,Edge39,Edge107,Edge114]
FEATURE [Part::Fillet] Fillet001
  Base = -> Chamfer037
  Edges = 2 edges r=8: [Edge160,Edge173]
FEATURE [Part::Chamfer] Chamfer038
  Base = -> Fillet001
  Edges = 2 edges r=2: [Edge237,Edge262]
FEATURE [Part::Chamfer] Chamfer039
  Base = -> Chamfer038
  Edges = 2 edges r=1: [Edge1,Edge5]
FEATURE [Part::Chamfer] Chamfer040
  Base = -> Chamfer039
  Edges = 1 edges r=1: [Edge139]
FEATURE [Part::Chamfer] Chamfer041
  Base = -> Chamfer040
  Edges = 1 edges r=1: [Edge10]
FEATURE [Part::Chamfer] Chamfer042
  Base = -> Chamfer041
  Edges = 1 edges r=1: [Edge14]
FEATURE [Part::Chamfer] Chamfer043
  Base = -> Chamfer042
  Edges = 1 edges r=1: [Edge16]
FEATURE [Part::Chamfer] Chamfer044
  Base = -> Chamfer043
  Edges = 1 edges r=1: [Edge4]
FEATURE [Mesh::Feature] Mesh004  label="novo_moto_holder_AMT (Meshed)"
FEATURE [Part::Cylinder] Cylinder349  label="Válec349"
  Angle = 360
  AttacherType = Attacher::AttachEngine3D
  Height = 50
  Placement = pos=(0,100,66) rot=(0,1,0;1.5708rad)
  Radius = 2.5
FEATURE [Part::Box] Box164  label="Krychle164"
  AttacherType = Attacher::AttachEngine3D
  Height = 40
  Length = 56.5
  Placement = pos=(-28.25,-28.25,34) rot=(0,0,1;0rad)
  Width = 56.5
FEATURE [Part::Box] Box165  label="Krychle165"
  AttacherType = Attacher::AttachEngine3D
  Height = 58
  Length = 20
  Placement = pos=(-10,-45.25,26) rot=(0,0,1;0rad)
  Width = 10
FEATURE [Part::Box] Box166  label="Krychle166"
  AttacherType = Attacher::AttachEngine3D
  Height = 20
  Length = 28.8
  Placement = pos=(-14.4,-8,34) rot=(0,0,1;0rad)
  Width = 43.38
FEATURE [Part::Cylinder] Cylinder350  label="Válec350"
  Angle = 360
  AttacherType = Attacher::AttachEngine3D
  Height = 12
  Placement = pos=(0,-32.55,100) rot=(0,1,0;1.5708rad)
  Radius = 5
FEATURE [Part::Box] Box167  label="Krychle167"
  AttacherType = Attacher::AttachEngine3D
  Height = 6
  Length = 8
  Placement = pos=(3,-48,34) rot=(0,0,1;0rad)
  Width = 2
FEATURE [Part::Box] Box168  label="Krychle168"
  AttacherType = Attacher::AttachEngine3D
  Height = 58
  Length = 34
  Placement = pos=(-17,-36.25,26) rot=(0,0,1;0rad)
  Width = 8
FEATURE [Part::Cylinder] Cylinder351  label="Válec351"
  Angle = 360
  AttacherType = Attacher::AttachEngine3D
  Height = 20
  Placement = pos=(-7,-34,73) rot=(1,0,0;1.5708rad)
  Radius = 1.5
FEATURE [Part::Box] Box169  label="Krychle169"
  AttacherType = Attacher::AttachEngine3D
  Height = 6
  Length = 8
  Placement = pos=(-11,-48,34) rot=(0,0,1;0rad)
  Width = 2
FEATURE [Part::Box] Box170  label="Krychle170"
  AttacherType = Attacher::AttachEngine3D
  Height = 16
  Length = 64
  Placement = pos=(-32,-32,34) rot=(0,0,1;0rad)
  Width = 64
FEATURE [Part::Cut] Cut163
  Base = -> Box170
  Tool = -> Box164
FEATURE [Part::Cylinder] Cylinder352  label="Válec352"
  Angle = 360
  AttacherType = Attacher::AttachEngine3D
  Height = 20
  Placement = pos=(7,-34,73) rot=(1,0,0;1.5708rad)
  Radius = 1.5
FEATURE [Part::Cylinder] Cylinder353  label="Válec353"
  Angle = 360
  AttacherType = Attacher::AttachEngine3D
  Height = 20
  Placement = pos=(-7,-34,37) rot=(1,0,0;1.5708rad)
  Radius = 1.5
FEATURE [Part::Box] Box171  label="Krychle171"
  AttacherType = Attacher::AttachEngine3D
  Height = 6
  Length = 8
  Placement = pos=(3,-48,70) rot=(0,0,1;0rad)
  Width = 2
FEATURE [Part::Cylinder] Cylinder354  label="Válec354"
  Angle = 360
  AttacherType = Attacher::AttachEngine3D
  Height = 12
  Placement = pos=(0,-32.55,100) rot=(0.57735,-0.57735,-0.57735;4.18879rad)
  Radius = 5
FEATURE [Part::Compound] Compound313
  Links = -> [Cylinder349]
  Placement = pos=(0,0,100) rot=(0,0,1;0rad)
FEATURE [Part::Cut] Cut159
  Base = -> Box168
  Tool = -> Compound313
FEATURE [Part::Compound] Compound320
  Links = -> [Cylinder354,Cylinder350]
FEATURE [Part::Cut] Cut165
  Base = -> Cut159
  Tool = -> Compound320
FEATURE [Part::Compound] Compound326  label="hrubo_holder018"
  Links = -> [Cut165,Cut163]
FEATURE [Part::Compound] Compound325  label="hrubo_holder017"
  Links = -> [Box165,Compound326]
FEATURE [Part::Cut] Cut157
  Base = -> Compound325
  Placement = pos=(-29,18,30) rot=(0,0,1;0rad)
  Tool = -> Box166
FEATURE [Part::Compound] Compound314
  Links = -> [Cut157]
  Placement = pos=(29,-18,-30) rot=(0,0,1;0rad)
FEATURE [Part::Compound] Compound321  label="hrubo_holder_nuovo005"
  Links = -> [Compound314]
FEATURE [Part::Compound] Compound323  label="hrubo_holder016"
  Links = -> [Compound321]
FEATURE [Part::Cylinder] Cylinder355  label="Válec355"
  Angle = 360
  AttacherType = Attacher::AttachEngine3D
  Height = 20
  Placement = pos=(0,0,15) rot=(0,0,1;0rad)
  Radius = 12
FEATURE [Part::Cylinder] Cylinder356  label="Válec356"
  Angle = 360
  AttacherType = Attacher::AttachEngine3D
  Height = 4
  Placement = pos=(23.55,23.55,26) rot=(0,0,1;0rad)
  Radius = 5
FEATURE [Part::Cylinder] Cylinder357  label="Válec357"
  Angle = 360
  AttacherType = Attacher::AttachEngine3D
  Height = 30
  Placement = pos=(-1.2e-14,-16,2) rot=(0,0,1;1.96349rad)
  Radius = 1.5
FEATURE [Part::Box] Box172  label="Krychle172"
  AttacherType = Attacher::AttachEngine3D
  Height = 3
  Length = 16
  Placement = pos=(-33.45,-27.55,31) rot=(0,0,1;0rad)
  Width = 8
FEATURE [Part::Cylinder] Cylinder358  label="Válec358"
  Angle = 360
  AttacherType = Attacher::AttachEngine3D
  Height = 3
  Placement = pos=(-16,7e-15,2) rot=(0,0,1;0.392699rad)
  Radius = 3
FEATURE [Part::Cylinder] Cylinder359  label="Válec359"
  Angle = 360
  AttacherType = Attacher::AttachEngine3D
  Height = 3
  Placement = pos=(2e-15,16,2) rot=(0,0,-1;1.1781rad)
  Radius = 3
FEATURE [Part::Cylinder] Cylinder360  label="Válec360"
  Angle = 360
  AttacherType = Attacher::AttachEngine3D
  Height = 30
  Placement = pos=(-16,7e-15,2) rot=(0,0,1;0.392699rad)
  Radius = 1.5
FEATURE [Part::Cylinder] Cylinder361  label="Válec361"
  Angle = 360
  AttacherType = Attacher::AttachEngine3D
  Height = 20
  Placement = pos=(-23.55,23.55,20) rot=(0,0,1;0rad)
  Radius = 2.5
FEATURE [Part::Cylinder] Cylinder362  label="Válec362"
  Angle = 360
  AttacherType = Attacher::AttachEngine3D
  Height = 20
  Placement = pos=(7,-34,37) rot=(1,0,0;1.5708rad)
  Radius = 1.5
FEATURE [Part::Compound] Compound319
  Links = -> [Cylinder362,Cylinder353,Cylinder352,Cylinder351]
FEATURE [Part::Cut] Cut158
  Base = -> Compound323
  Tool = -> Compound319
FEATURE [Part::Box] Box173  label="Krychle173"
  AttacherType = Attacher::AttachEngine3D
  Height = 8
  Length = 64
  Placement = pos=(-32,-32,26) rot=(0,0,1;0rad)
  Width = 64
FEATURE [Part::Cylinder] Cylinder363  label="Válec363"
  Angle = 360
  AttacherType = Attacher::AttachEngine3D
  Height = 20
  Placement = pos=(-23.55,-23.55,20) rot=(0,0,1;0rad)
  Radius = 2.5
FEATURE [Part::Box] Box174  label="Krychle174"
  AttacherType = Attacher::AttachEngine3D
  Height = 3
  Length = 16
  Placement = pos=(-33.45,19.55,31) rot=(0,0,1;0rad)
  Width = 8
FEATURE [Part::Box] Box175  label="Krychle175"
  AttacherType = Attacher::AttachEngine3D
  Height = 3
  Length = 16
  Placement = pos=(17.55,-27.55,31) rot=(0,0,1;0rad)
  Width = 8
FEATURE [Part::Box] Box176  label="Krychle176"
  AttacherType = Attacher::AttachEngine3D
  Height = 6
  Length = 8
  Placement = pos=(-11,-48,70) rot=(0,0,1;0rad)
  Width = 2
FEATURE [Part::Compound] Compound315
  Links = -> [Box167,Box169,Box171,Box176]
  Placement = pos=(0,9.75,0) rot=(0,0,1;0rad)
FEATURE [Part::Cut] Cut164  label="motor_holder003"
  Base = -> Cut158
  Tool = -> Compound315
FEATURE [Part::Cylinder] Cylinder364  label="Válec364"
  Angle = 360
  AttacherType = Attacher::AttachEngine3D
  Height = 4
  Placement = pos=(-23.55,-23.55,26) rot=(0,0,1;0rad)
  Radius = 5
FEATURE [Part::Cylinder] Cylinder365  label="Válec365"
  Angle = 360
  AttacherType = Attacher::AttachEngine3D
  Height = 4
  Placement = pos=(23.55,-23.55,26) rot=(0,0,1;0rad)
  Radius = 5
FEATURE [Part::Box] Box177  label="Krychle177"
  AttacherType = Attacher::AttachEngine3D
  Height = 3
  Length = 16
  Placement = pos=(17.55,19.55,31) rot=(0,0,1;0rad)
  Width = 8
FEATURE [Part::Compound] Compound318
  Links = -> [Box177,Box175,Box174,Box172]
FEATURE [Part::Cylinder] Cylinder366  label="Válec366"
  Angle = 360
  AttacherType = Attacher::AttachEngine3D
  Height = 20
  Placement = pos=(23.55,-23.55,20) rot=(0,0,1;0rad)
  Radius = 2.5
FEATURE [Part::Cylinder] Cylinder367  label="Válec367"
  Angle = 360
  AttacherType = Attacher::AttachEngine3D
  Height = 3
  Placement = pos=(-1.2e-14,-16,2) rot=(0,0,1;1.96349rad)
  Radius = 3
FEATURE [Part::Cylinder] Cylinder368  label="Válec368"
  Angle = 360
  AttacherType = Attacher::AttachEngine3D
  Height = 3
  Placement = pos=(16,0,2) rot=(0,0,1;3.53429rad)
  Radius = 3
FEATURE [Part::Compound] Compound322
  Links = -> [Cylinder367,Cylinder358,Cylinder359,Cylinder368]
  Placement = pos=(0,0,29) rot=(0,0,1;0.785398rad)
FEATURE [Part::Cylinder] Cylinder369  label="Válec369"
  Angle = 360
  AttacherType = Attacher::AttachEngine3D
  Height = 20
  Placement = pos=(23.55,23.55,20) rot=(0,0,1;0rad)
  Radius = 2.5
FEATURE [Part::Compound] Compound316
  Links = -> [Cylinder369,Cylinder361,Cylinder363,Cylinder366]
FEATURE [Part::Cylinder] Cylinder370  label="Válec370"
  Angle = 360
  AttacherType = Attacher::AttachEngine3D
  Height = 4
  Placement = pos=(-23.55,23.55,26) rot=(0,0,1;0rad)
  Radius = 5
FEATURE [Part::Compound] Compound317
  Links = -> [Cylinder364,Cylinder356,Cylinder365,Cylinder370]
  Placement = pos=(0,0,-50) rot=(0,0,1;0rad)
FEATURE [Part::Cylinder] Cylinder371  label="Válec371"
  Angle = 360
  AttacherType = Attacher::AttachEngine3D
  Height = 30
  Placement = pos=(2e-15,16,2) rot=(0,0,-1;1.1781rad)
  Radius = 1.5
FEATURE [Part::Cylinder] Cylinder372  label="Válec372"
  Angle = 360
  AttacherType = Attacher::AttachEngine3D
  Height = 30
  Placement = pos=(16,0,2) rot=(0,0,1;3.53429rad)
  Radius = 1.5
FEATURE [Part::Compound] Compound324
  Links = -> [Cylinder357,Cylinder360,Cylinder371,Cylinder372]
  Placement = pos=(0,0,14) rot=(0,0,1;0.785398rad)
FEATURE [Part::Cut] Cut161
  Base = -> Box173
  Tool = -> Compound324
FEATURE [Part::Cut] Cut160
  Base = -> Cut161
  Tool = -> Compound322
FEATURE [Part::Cut] Cut155
  Base = -> Cut160
  Tool = -> Compound316
FEATURE [Part::Cut] Cut162
  Base = -> Cut155
  Tool = -> Compound317
FEATURE [Part::Cut] Cut156
  Base = -> Cut162
  Tool = -> Cylinder355
FEATURE [Part::Cut] Cut166
  Base = -> Cut156
  Tool = -> Compound318
FEATURE [Part::Compound] Compound327  label="novo_moto_holder_hrubo002"
  Links = -> [Cut164,Cut166]
FEATURE [Part::Box] Box619  label="Krychle619"
  AttacherType = Attacher::AttachEngine3D
  Height = 59
  Length = 20
  Placement = pos=(-10,-53,26) rot=(0,0,1;0rad)
  Width = 17
FEATURE [Part::Box] Box623  label="Krychle623"
  AttacherType = Attacher::AttachEngine3D
  Height = 80
  Length = 34
  Placement = pos=(-17,-36.25,26) rot=(0,0,1;0rad)
  Width = 8
FEATURE [Part::Cylinder] Cylinder1583  label="Válec1583"
  Angle = 360
  AttacherType = Attacher::AttachEngine3D
  Height = 40
  Placement = pos=(-7,-34,37) rot=(1,0,0;1.5708rad)
  Radius = 1.5
FEATURE [Part::Cylinder] Cylinder1581  label="Válec1581"
  Angle = 360
  AttacherType = Attacher::AttachEngine3D
  Height = 40
  Placement = pos=(7,-34,73) rot=(1,0,0;1.5708rad)
  Radius = 1.5
FEATURE [Part::Box] Box625  label="Krychle625"
  AttacherType = Attacher::AttachEngine3D
  Height = 6
  Length = 8
  Placement = pos=(3,-48,34) rot=(0,0,1;0rad)
  Width = 2
FEATURE [Part::Box] Box621  label="Krychle621"
  AttacherType = Attacher::AttachEngine3D
  Height = 6
  Length = 8
  Placement = pos=(3,-48,70) rot=(0,0,1;0rad)
  Width = 2
FEATURE [Part::Box] Box624  label="Krychle624"
  AttacherType = Attacher::AttachEngine3D
  Height = 6
  Length = 8
  Placement = pos=(-11,-48,34) rot=(0,0,1;0rad)
  Width = 2
FEATURE [Part::Cylinder] Cylinder1582  label="Válec1582"
  Angle = 360
  AttacherType = Attacher::AttachEngine3D
  Height = 40
  Placement = pos=(-7,-34,73) rot=(1,0,0;1.5708rad)
  Radius = 1.5
FEATURE [Part::Box] Box627  label="Krychle627"
  AttacherType = Attacher::AttachEngine3D
  Height = 6
  Length = 8
  Placement = pos=(-11,-48,70) rot=(0,0,1;0rad)
  Width = 2
FEATURE [Part::Cylinder] Cylinder1593  label="Válec1593"
  Angle = 360
  AttacherType = Attacher::AttachEngine3D
  Height = 40
  Placement = pos=(7,-34,37) rot=(1,0,0;1.5708rad)
  Radius = 1.5
FEATURE [Part::Compound] Compound328
  Links = -> [Cylinder1593,Cylinder1583,Cylinder1581,Cylinder1582]
  Placement = pos=(0,-5,0) rot=(0,0,1;0rad)
FEATURE [Part::Compound] Compound794
  Links = -> [Box625,Box624,Box621,Box627]
  Placement = pos=(0,-1,0) rot=(0,0,1;0rad)
FEATURE [Part::Cut] Cut167
  Base = -> Box619
  Tool = -> Compound328
FEATURE [Part::Cut] Cut168
  Base = -> Cut167
  Tool = -> Compound794
FEATURE [Part::Box] Box628  label="Krychle628"
  AttacherType = Attacher::AttachEngine3D
  Height = 20
  Length = 28.8
  Placement = pos=(-14.4,-8,34) rot=(0,0,1;0rad)
  Width = 43.38
FEATURE [Part::Box] Box629  label="Krychle629"
  AttacherType = Attacher::AttachEngine3D
  Height = 40
  Length = 56.5
  Placement = pos=(-28.25,-28.25,34) rot=(0,0,1;0rad)
  Width = 56.5
FEATURE [Part::Box] Box630  label="Krychle630"
  AttacherType = Attacher::AttachEngine3D
  Height = 16
  Length = 64
  Placement = pos=(-32,-32,34) rot=(0,0,1;0rad)
  Width = 64
FEATURE [Part::Cut] Cut169
  Base = -> Box630
  Tool = -> Box629
FEATURE [Part::Cut] Cut170
  Base = -> Cut169
  Tool = -> Box628
FEATURE [Part::Cylinder] Cylinder774  label="Válec774"
  Angle = 360
  AttacherType = Attacher::AttachEngine3D
  Height = 20
  Placement = pos=(15.75,114,38.52) rot=(0,0.707107,0.707107;3.14159rad)
  Radius = 1.5
FEATURE [Part::Cylinder] Cylinder776  label="Válec776"
  Angle = 360
  AttacherType = Attacher::AttachEngine3D
  Height = 20
  Placement = pos=(15.75,114,59.48) rot=(0,0.707107,0.707107;3.14159rad)
  Radius = 1.5
FEATURE [Part::Compound] Compound536
  Links = -> [Cylinder774,Cylinder776]
  Placement = pos=(-49,0,-96) rot=(0.57735,0.57735,0.57735;2.0944rad)
FEATURE [Part::Box] Box631  label="Krychle631"
  AttacherType = Attacher::AttachEngine3D
  Height = 9
  Length = 10
  Placement = pos=(-58,-10,63) rot=(0,0,1;0rad)
  Width = 48
FEATURE [Part::Cylinder] Cylinder1594  label="Válec1594"
  Angle = 360
  AttacherType = Attacher::AttachEngine3D
  Height = 50
  Placement = pos=(23.55,23.55,20) rot=(0,0,1;0rad)
  Radius = 2.5
FEATURE [Part::Cylinder] Cylinder1595  label="Válec1595"
  Angle = 360
  AttacherType = Attacher::AttachEngine3D
  Height = 50
  Placement = pos=(-23.55,23.55,20) rot=(0,0,1;0rad)
  Radius = 2.5
FEATURE [Part::Cylinder] Cylinder1596  label="Válec1596"
  Angle = 360
  AttacherType = Attacher::AttachEngine3D
  Height = 50
  Placement = pos=(23.55,-23.55,20) rot=(0,0,1;0rad)
  Radius = 2.5
FEATURE [Part::Box] Box632  label="Krychle632"
  AttacherType = Attacher::AttachEngine3D
  Height = 9
  Length = 38
  Placement = pos=(-48,-10,63) rot=(0,0,1;0rad)
  Width = 10
FEATURE [Part::Cylinder] Cylinder1597  label="Válec1597"
  Angle = 360
  AttacherType = Attacher::AttachEngine3D
  Height = 50
  Placement = pos=(-23.55,-23.55,20) rot=(0,0,1;0rad)
  Radius = 2.5
FEATURE [Part::Compound] Compound797
  Links = -> [Cylinder1594,Cylinder1596,Cylinder1597,Cylinder1595]
FEATURE [Part::Box] Box633  label="Krychle633"
  AttacherType = Attacher::AttachEngine3D
  Height = 9
  Length = 10
  Placement = pos=(-10,-10,63) rot=(0,0,1;0rad)
  Width = 48
FEATURE [Part::Box] Box634  label="Krychle634"
  AttacherType = Attacher::AttachEngine3D
  Height = 9
  Length = 14.6
  Placement = pos=(-58,38,63) rot=(0,0,1;0rad)
  Width = 10
FEATURE [Part::Box] Box635  label="Krychle635"
  AttacherType = Attacher::AttachEngine3D
  Height = 9
  Length = 14.62
  Placement = pos=(-14.6,38,63) rot=(0,0,1;0rad)
  Width = 10
FEATURE [Part::Compound] Compound796
  Links = -> [Box634,Box633,Box631,Box635,Box632]
  Placement = pos=(29,-19,-4) rot=(0,0,1;0rad)
FEATURE [Part::Cut] Cut172
  Base = -> Compound796
  Placement = pos=(0,0,-25) rot=(0,0,1;0rad)
  Tool = -> Compound797
FEATURE [Part::Chamfer] Chamfer050
  Base = -> Cut172
  Edges = 1 edges r=2: [Edge46]
FEATURE [Part::Chamfer] Chamfer051  label="podlo_AMT001"
  Base = -> Chamfer050
  Edges = 1 edges r=2: [Edge24]
FEATURE [Part::Box] Box636  label="Krychle636"
  AttacherType = Attacher::AttachEngine3D
  Height = 3
  Length = 16
  Placement = pos=(-33.45,-27.55,31) rot=(0,0,1;0rad)
  Width = 8
FEATURE [Part::Cylinder] Cylinder1598  label="Válec1598"
  Angle = 360
  AttacherType = Attacher::AttachEngine3D
  Height = 4
  Placement = pos=(23.55,23.55,26) rot=(0,0,1;0rad)
  Radius = 5
FEATURE [Part::Cylinder] Cylinder1599  label="Válec1599"
  Angle = 360
  AttacherType = Attacher::AttachEngine3D
  Height = 30
  Placement = pos=(-1.2e-14,-16,2) rot=(0,0,1;1.96349rad)
  Radius = 1.5
FEATURE [Part::Cylinder] Cylinder1600  label="Válec1600"
  Angle = 360
  AttacherType = Attacher::AttachEngine3D
  Height = 20
  Placement = pos=(0,0,15) rot=(0,0,1;0rad)
  Radius = 12
FEATURE [Part::Cylinder] Cylinder1601  label="Válec1601"
  Angle = 360
  AttacherType = Attacher::AttachEngine3D
  Height = 3
  Placement = pos=(2e-15,16,2) rot=(0,0,-1;1.1781rad)
  Radius = 3
FEATURE [Part::Box] Box637  label="Krychle637"
  AttacherType = Attacher::AttachEngine3D
  Height = 3
  Length = 16
  Placement = pos=(17.55,19.55,31) rot=(0,0,1;0rad)
  Width = 8
FEATURE [Part::Cylinder] Cylinder1602  label="Válec1602"
  Angle = 360
  AttacherType = Attacher::AttachEngine3D
  Height = 20
  Placement = pos=(23.55,23.55,20) rot=(0,0,1;0rad)
  Radius = 2.5
FEATURE [Part::Cylinder] Cylinder1603  label="Válec1603"
  Angle = 360
  AttacherType = Attacher::AttachEngine3D
  Height = 30
  Placement = pos=(-16,7e-15,2) rot=(0,0,1;0.392699rad)
  Radius = 1.5
FEATURE [Part::Cylinder] Cylinder1604  label="Válec1604"
  Angle = 360
  AttacherType = Attacher::AttachEngine3D
  Height = 20
  Placement = pos=(-23.55,23.55,20) rot=(0,0,1;0rad)
  Radius = 2.5
FEATURE [Part::Cylinder] Cylinder1605  label="Válec1605"
  Angle = 360
  AttacherType = Attacher::AttachEngine3D
  Height = 4
  Placement = pos=(23.55,-23.55,26) rot=(0,0,1;0rad)
  Radius = 5
FEATURE [Part::Box] Box638  label="Krychle638"
  AttacherType = Attacher::AttachEngine3D
  Height = 8
  Length = 64
  Placement = pos=(-32,-32,26) rot=(0,0,1;0rad)
  Width = 64
FEATURE [Part::Cylinder] Cylinder1606  label="Válec1606"
  Angle = 360
  AttacherType = Attacher::AttachEngine3D
  Height = 3
  Placement = pos=(16,0,2) rot=(0,0,1;3.53429rad)
  Radius = 3
FEATURE [Part::Box] Box639  label="Krychle639"
  AttacherType = Attacher::AttachEngine3D
  Height = 3
  Length = 16
  Placement = pos=(-33.45,19.55,31) rot=(0,0,1;0rad)
  Width = 8
FEATURE [Part::Cylinder] Cylinder1607  label="Válec1607"
  Angle = 360
  AttacherType = Attacher::AttachEngine3D
  Height = 20
  Placement = pos=(23.55,-23.55,20) rot=(0,0,1;0rad)
  Radius = 2.5
FEATURE [Part::Cylinder] Cylinder1608  label="Válec1608"
  Angle = 360
  AttacherType = Attacher::AttachEngine3D
  Height = 20
  Placement = pos=(-23.55,-23.55,20) rot=(0,0,1;0rad)
  Radius = 2.5
FEATURE [Part::Compound] Compound798
  Links = -> [Cylinder1602,Cylinder1604,Cylinder1608,Cylinder1607]
FEATURE [Part::Box] Box640  label="Krychle640"
  AttacherType = Attacher::AttachEngine3D
  Height = 3
  Length = 16
  Placement = pos=(17.55,-27.55,31) rot=(0,0,1;0rad)
  Width = 8
FEATURE [Part::Compound] Compound800
  Links = -> [Box637,Box640,Box639,Box636]
FEATURE [Part::Cylinder] Cylinder1609  label="Válec1609"
  Angle = 360
  AttacherType = Attacher::AttachEngine3D
  Height = 3
  Placement = pos=(-16,7e-15,2) rot=(0,0,1;0.392699rad)
  Radius = 3
FEATURE [Part::Cylinder] Cylinder1610  label="Válec1610"
  Angle = 360
  AttacherType = Attacher::AttachEngine3D
  Height = 4
  Placement = pos=(-23.55,-23.55,26) rot=(0,0,1;0rad)
  Radius = 5
FEATURE [Part::Cylinder] Cylinder1611  label="Válec1611"
  Angle = 360
  AttacherType = Attacher::AttachEngine3D
  Height = 3
  Placement = pos=(-1.2e-14,-16,2) rot=(0,0,1;1.96349rad)
  Radius = 3
FEATURE [Part::Compound] Compound801
  Links = -> [Cylinder1611,Cylinder1609,Cylinder1601,Cylinder1606]
  Placement = pos=(0,0,29) rot=(0,0,1;0.785398rad)
FEATURE [Part::Cylinder] Cylinder1612  label="Válec1612"
  Angle = 360
  AttacherType = Attacher::AttachEngine3D
  Height = 4
  Placement = pos=(-23.55,23.55,26) rot=(0,0,1;0rad)
  Radius = 5
FEATURE [Part::Compound] Compound799
  Links = -> [Cylinder1610,Cylinder1598,Cylinder1605,Cylinder1612]
  Placement = pos=(0,0,-50) rot=(0,0,1;0rad)
FEATURE [Part::Cylinder] Cylinder1613  label="Válec1613"
  Angle = 360
  AttacherType = Attacher::AttachEngine3D
  Height = 30
  Placement = pos=(2e-15,16,2) rot=(0,0,-1;1.1781rad)
  Radius = 1.5
FEATURE [Part::Cylinder] Cylinder1614  label="Válec1614"
  Angle = 360
  AttacherType = Attacher::AttachEngine3D
  Height = 30
  Placement = pos=(16,0,2) rot=(0,0,1;3.53429rad)
  Radius = 1.5
FEATURE [Part::Compound] Compound802
  Links = -> [Cylinder1599,Cylinder1603,Cylinder1613,Cylinder1614]
  Placement = pos=(0,0,14) rot=(0,0,1;0.785398rad)
FEATURE [Part::Cut] Cut173
  Base = -> Box638
  Tool = -> Compound802
FEATURE [Part::Cut] Cut174
  Base = -> Cut173
  Tool = -> Compound801
FEATURE [Part::Cut] Cut177
  Base = -> Cut174
  Tool = -> Compound798
FEATURE [Part::Cut] Cut175
  Base = -> Cut177
  Tool = -> Compound799
FEATURE [Part::Cut] Cut176
  Base = -> Cut175
  Tool = -> Cylinder1600
FEATURE [Part::Cut] Cut178
  Base = -> Cut176
  Tool = -> Compound800
FEATURE [Part::Cut] Cut179
  Base = -> Cut178
  Tool = -> Compound536
FEATURE [Part::Compound] Compound803
  Links = -> [Cut179,Cut170]
FEATURE [Part::Chamfer] Chamfer052
  Base = -> Compound803
  Edges = 4 edges r=3: [Edge10,Edge12,Edge106,Edge108]
FEATURE [Part::Chamfer] Chamfer053
  Base = -> Chamfer052
  Edges = 4 edges r=3: [Edge69,Edge76,Edge148,Edge150]
FEATURE [Part::Fillet] Fillet002
  Base = -> Cut168
  Edges = 2 edges r=8.9: [Edge2,Edge21]
FEATURE [Part::Chamfer] Chamfer054
  Base = -> Chamfer053
  Edges = 5 edges r=1: [Edge118,Edge120,Edge122,Edge130,Edge132]
FEATURE [Part::Chamfer] Chamfer055
  Base = -> Box623
  Edges = 2 edges r=8: [Edge2,Edge6]
FEATURE [Part::Chamfer] Chamfer056
  Base = -> Chamfer055
  Edges = 1 edges r=4: [Edge8]
FEATURE [Part::Fillet] Fillet003
  Base = -> Chamfer056
  Edges = 2 edges r=4: [Edge4,Edge6]
FEATURE [Part::Compound] Compound804  label="J-max_moto-hold-old"
  Links = -> [Chamfer051,Fillet002,Chamfer054,Fillet003]
FEATURE [Mesh::Feature] Mesh005  label="J-max_moto-hold (Meshed)"
FEATURE [Part::Box] Box641  label="Krychle641"
  AttacherType = Attacher::AttachEngine3D
  Height = 9
  Length = 28.8
  Placement = pos=(-14.4,-8,59) rot=(0,0,1;0rad)
  Width = 43.38
FEATURE [Part::Box] Box642  label="Krychle642"
  AttacherType = Attacher::AttachEngine3D
  Height = 9
  Length = 64
  Placement = pos=(-32,-32,34) rot=(0,0,1;0rad)
  Width = 64
FEATURE [Part::Cylinder] Cylinder1615  label="Válec1615"
  Angle = 360
  AttacherType = Attacher::AttachEngine3D
  Height = 40
  Placement = pos=(7,-34,37) rot=(1,0,0;1.5708rad)
  Radius = 1.5
FEATURE [Part::Box] Box643  label="Krychle643"
  AttacherType = Attacher::AttachEngine3D
  Height = 40
  Length = 56.5
  Placement = pos=(-28.25,-28.25,34) rot=(0,0,1;0rad)
  Width = 56.5
FEATURE [Part::Cut] Cut184
  Base = -> Box642
  Tool = -> Box643
FEATURE [Part::Box] Box644  label="Krychle644"
  AttacherType = Attacher::AttachEngine3D
  Height = 59
  Length = 20
  Placement = pos=(-10,-53,26) rot=(0,0,1;0rad)
  Width = 17
FEATURE [Part::Cylinder] Cylinder1616  label="Válec1616"
  Angle = 360
  AttacherType = Attacher::AttachEngine3D
  Height = 20
  Placement = pos=(15.75,114,59.48) rot=(0,0.707107,0.707107;3.14159rad)
  Radius = 1.5
FEATURE [Part::Cylinder] Cylinder1617  label="Válec1617"
  Angle = 360
  AttacherType = Attacher::AttachEngine3D
  Height = 40
  Placement = pos=(7,-34,73) rot=(1,0,0;1.5708rad)
  Radius = 1.5
FEATURE [Part::Box] Box645  label="Krychle645"
  AttacherType = Attacher::AttachEngine3D
  Height = 6
  Length = 8
  Placement = pos=(3,-48,70) rot=(0,0,1;0rad)
  Width = 2
FEATURE [Part::Box] Box646  label="Krychle646"
  AttacherType = Attacher::AttachEngine3D
  Height = 6
  Length = 8
  Placement = pos=(3,-48,34) rot=(0,0,1;0rad)
  Width = 2
FEATURE [Part::Box] Box647  label="Krychle647"
  AttacherType = Attacher::AttachEngine3D
  Height = 6
  Length = 8
  Placement = pos=(-11,-48,34) rot=(0,0,1;0rad)
  Width = 2
FEATURE [Part::Cylinder] Cylinder1618  label="Válec1618"
  Angle = 360
  AttacherType = Attacher::AttachEngine3D
  Height = 40
  Placement = pos=(-7,-34,73) rot=(1,0,0;1.5708rad)
  Radius = 1.5
FEATURE [Part::Box] Box648  label="Krychle648"
  AttacherType = Attacher::AttachEngine3D
  Height = 6
  Length = 8
  Placement = pos=(-11,-48,70) rot=(0,0,1;0rad)
  Width = 2
FEATURE [Part::Cylinder] Cylinder1619  label="Válec1619"
  Angle = 360
  AttacherType = Attacher::AttachEngine3D
  Height = 30
  Placement = pos=(-1.2e-14,-16,2) rot=(0,0,1;1.96349rad)
  Radius = 1.5
FEATURE [Part::Cylinder] Cylinder1620  label="Válec1620"
  Angle = 360
  AttacherType = Attacher::AttachEngine3D
  Height = 40
  Placement = pos=(-7,-34,37) rot=(1,0,0;1.5708rad)
  Radius = 1.5
FEATURE [Part::Box] Box649  label="Krychle649"
  AttacherType = Attacher::AttachEngine3D
  Height = 3
  Length = 16
  Placement = pos=(-33.45,-27.55,31) rot=(0,0,1;0rad)
  Width = 8
FEATURE [Part::Cylinder] Cylinder1621  label="Válec1621"
  Angle = 360
  AttacherType = Attacher::AttachEngine3D
  Height = 20
  Placement = pos=(15.75,114,38.52) rot=(0,0.707107,0.707107;3.14159rad)
  Radius = 1.5
FEATURE [Part::Box] Box650  label="Krychle650"
  AttacherType = Attacher::AttachEngine3D
  Height = 3
  Length = 16
  Placement = pos=(17.55,19.55,31) rot=(0,0,1;0rad)
  Width = 8
FEATURE [Part::Cylinder] Cylinder1622  label="Válec1622"
  Angle = 360
  AttacherType = Attacher::AttachEngine3D
  Height = 4
  Placement = pos=(23.55,23.55,26) rot=(0,0,1;0rad)
  Radius = 5
FEATURE [Part::Cylinder] Cylinder1623  label="Válec1623"
  Angle = 360
  AttacherType = Attacher::AttachEngine3D
  Height = 30
  Placement = pos=(-16,7e-15,2) rot=(0,0,1;0.392699rad)
  Radius = 1.5
FEATURE [Part::Cylinder] Cylinder1624  label="Válec1624"
  Angle = 360
  AttacherType = Attacher::AttachEngine3D
  Height = 20
  Placement = pos=(-23.55,-23.55,20) rot=(0,0,1;0rad)
  Radius = 2.5
FEATURE [Part::Cylinder] Cylinder1625  label="Válec1625"
  Angle = 360
  AttacherType = Attacher::AttachEngine3D
  Height = 20
  Placement = pos=(-23.55,23.55,20) rot=(0,0,1;0rad)
  Radius = 2.5
FEATURE [Part::Cylinder] Cylinder1626  label="Válec1626"
  Angle = 360
  AttacherType = Attacher::AttachEngine3D
  Height = 3
  Placement = pos=(-1.2e-14,-16,2) rot=(0,0,1;1.96349rad)
  Radius = 3
FEATURE [Part::Cylinder] Cylinder1627  label="Válec1627"
  Angle = 360
  AttacherType = Attacher::AttachEngine3D
  Height = 4
  Placement = pos=(23.55,-23.55,26) rot=(0,0,1;0rad)
  Radius = 5
FEATURE [Part::Box] Box651  label="Krychle651"
  AttacherType = Attacher::AttachEngine3D
  Height = 80
  Length = 34
  Placement = pos=(-17,-36.25,26) rot=(0,0,1;0rad)
  Width = 8
FEATURE [Part::Box] Box652  label="Krychle652"
  AttacherType = Attacher::AttachEngine3D
  Height = 20
  Length = 28.8
  Placement = pos=(-14.4,-8,34) rot=(0,0,1;0rad)
  Width = 43.38
FEATURE [Part::Cut] Cut182
  Base = -> Cut184
  Tool = -> Box652
FEATURE [Part::Chamfer] Chamfer059
  Base = -> Cut182
  Edges = 2 edges r=3: [Edge1,Edge3]
FEATURE [Part::Chamfer] Chamfer058
  Base = -> Chamfer059
  Edges = 2 edges r=3: [Edge37,Edge39]
FEATURE [Part::Chamfer] Chamfer061
  Base = -> Chamfer058
  Edges = 5 edges r=1.4: [Edge1,Edge3,Edge5,Edge13,Edge15]
FEATURE [Part::Cylinder] Cylinder1628  label="Válec1628"
  Angle = 360
  AttacherType = Attacher::AttachEngine3D
  Height = 20
  Placement = pos=(23.55,23.55,20) rot=(0,0,1;0rad)
  Radius = 2.5
FEATURE [Part::Cylinder] Cylinder1629  label="Válec1629"
  Angle = 360
  AttacherType = Attacher::AttachEngine3D
  Height = 3
  Placement = pos=(16,0,2) rot=(0,0,1;3.53429rad)
  Radius = 3
FEATURE [Part::Box] Box653  label="Krychle653"
  AttacherType = Attacher::AttachEngine3D
  Height = 8
  Length = 64
  Placement = pos=(-32,-32,26) rot=(0,0,1;0rad)
  Width = 64
FEATURE [Part::Cylinder] Cylinder1630  label="Válec1630"
  Angle = 360
  AttacherType = Attacher::AttachEngine3D
  Height = 20
  Placement = pos=(0,0,15) rot=(0,0,1;0rad)
  Radius = 12
FEATURE [Part::Box] Box654  label="Krychle654"
  AttacherType = Attacher::AttachEngine3D
  Height = 3
  Length = 16
  Placement = pos=(-33.45,19.55,31) rot=(0,0,1;0rad)
  Width = 8
FEATURE [Part::Cylinder] Cylinder1631  label="Válec1631"
  Angle = 360
  AttacherType = Attacher::AttachEngine3D
  Height = 3
  Placement = pos=(-16,7e-15,2) rot=(0,0,1;0.392699rad)
  Radius = 3
FEATURE [Part::Cylinder] Cylinder1632  label="Válec1632"
  Angle = 360
  AttacherType = Attacher::AttachEngine3D
  Height = 20
  Placement = pos=(23.55,-23.55,20) rot=(0,0,1;0rad)
  Radius = 2.5
FEATURE [Part::Cylinder] Cylinder1633  label="Válec1633"
  Angle = 360
  AttacherType = Attacher::AttachEngine3D
  Height = 30
  Placement = pos=(2e-15,16,2) rot=(0,0,-1;1.1781rad)
  Radius = 1.5
FEATURE [Part::Box] Box655  label="Krychle655"
  AttacherType = Attacher::AttachEngine3D
  Height = 3
  Length = 16
  Placement = pos=(17.55,-27.55,31) rot=(0,0,1;0rad)
  Width = 8
FEATURE [Part::Cylinder] Cylinder1634  label="Válec1634"
  Angle = 360
  AttacherType = Attacher::AttachEngine3D
  Height = 4
  Placement = pos=(-23.55,-23.55,26) rot=(0,0,1;0rad)
  Radius = 5
FEATURE [Part::Cylinder] Cylinder1635  label="Válec1635"
  Angle = 360
  AttacherType = Attacher::AttachEngine3D
  Height = 3
  Placement = pos=(2e-15,16,2) rot=(0,0,-1;1.1781rad)
  Radius = 3
FEATURE [Part::Cylinder] Cylinder1636  label="Válec1636"
  Angle = 360
  AttacherType = Attacher::AttachEngine3D
  Height = 4
  Placement = pos=(-23.55,23.55,26) rot=(0,0,1;0rad)
  Radius = 5
FEATURE [Part::Cylinder] Cylinder1637  label="Válec1637"
  Angle = 360
  AttacherType = Attacher::AttachEngine3D
  Height = 30
  Placement = pos=(16,0,2) rot=(0,0,1;3.53429rad)
  Radius = 1.5
FEATURE [Part::Compound] Compound805
  Links = -> [Box646,Box647,Box645,Box648]
  Placement = pos=(0,-1,0) rot=(0,0,1;0rad)
FEATURE [Part::Compound] Compound806
  Links = -> [Cylinder1626,Cylinder1631,Cylinder1635,Cylinder1629]
  Placement = pos=(0,0,29) rot=(0,0,1;0.785398rad)
FEATURE [Part::Compound] Compound807
  Links = -> [Cylinder1634,Cylinder1622,Cylinder1627,Cylinder1636]
  Placement = pos=(0,0,-50) rot=(0,0,1;0rad)
FEATURE [Part::Compound] Compound808
  Links = -> [Cylinder1619,Cylinder1623,Cylinder1633,Cylinder1637]
  Placement = pos=(0,0,14) rot=(0,0,1;0.785398rad)
FEATURE [Part::Cut] Cut180
  Base = -> Box653
  Tool = -> Compound808
FEATURE [Part::Cut] Cut189
  Base = -> Cut180
  Tool = -> Compound806
FEATURE [Part::Compound] Compound809
  Links = -> [Cylinder1621,Cylinder1616]
  Placement = pos=(-49,0,-96) rot=(0.57735,0.57735,0.57735;2.0944rad)
FEATURE [Part::Compound] Compound811
  Links = -> [Cylinder1615,Cylinder1620,Cylinder1617,Cylinder1618]
  Placement = pos=(0,-5,0) rot=(0,0,1;0rad)
FEATURE [Part::Cut] Cut185
  Base = -> Box644
  Tool = -> Compound811
FEATURE [Part::Cut] Cut186
  Base = -> Cut185
  Tool = -> Compound805
FEATURE [Part::Fillet] Fillet004
  Base = -> Cut186
  Edges = 2 edges r=8.9: [Edge2,Edge21]
FEATURE [Part::Compound] Compound812
  Links = -> [Cylinder1628,Cylinder1625,Cylinder1624,Cylinder1632]
FEATURE [Part::Cut] Cut187
  Base = -> Cut189
  Tool = -> Compound812
FEATURE [Part::Cut] Cut190
  Base = -> Cut187
  Tool = -> Compound807
FEATURE [Part::Cut] Cut181
  Base = -> Cut190
  Tool = -> Cylinder1630
FEATURE [Part::Compound] Compound813
  Links = -> [Box650,Box655,Box654,Box649]
  Placement = pos=(0,0,-3) rot=(0,0,1;0rad)
FEATURE [Part::Cut] Cut188
  Base = -> Cut181
  Tool = -> Compound813
FEATURE [Part::Cut] Cut183
  Base = -> Cut188
  Tool = -> Compound809
FEATURE [Part::Chamfer] Chamfer057
  Base = -> Cut183
  Edges = 2 edges r=3: [Edge1,Edge4]
FEATURE [Part::Chamfer] Chamfer060
  Base = -> Chamfer057
  Edges = 2 edges r=3: [Edge67,Edge68]
FEATURE [Part::Chamfer] Chamfer063
  Base = -> Box651
  Edges = 2 edges r=8: [Edge2,Edge6]
FEATURE [Part::Chamfer] Chamfer062
  Base = -> Chamfer063
  Edges = 1 edges r=4: [Edge8]
FEATURE [Part::Fillet] Fillet005
  Base = -> Chamfer062
  Edges = 2 edges r=4: [Edge4,Edge6]
FEATURE [Part::Cylinder] Cylinder1638  label="Válec1638"
  Angle = 360
  AttacherType = Attacher::AttachEngine3D
  Height = 40
  Placement = pos=(-7,-34,73) rot=(1,0,0;1.5708rad)
  Radius = 1.5
FEATURE [Part::Box] Box656  label="Krychle656"
  AttacherType = Attacher::AttachEngine3D
  Height = 6
  Length = 8
  Placement = pos=(-11,-48,70) rot=(0,0,1;0rad)
  Width = 2
FEATURE [Part::Cylinder] Cylinder1639  label="Válec1639"
  Angle = 360
  AttacherType = Attacher::AttachEngine3D
  Height = 40
  Placement = pos=(7,-34,73) rot=(1,0,0;1.5708rad)
  Radius = 1.5
FEATURE [Part::Box] Box657  label="Krychle657"
  AttacherType = Attacher::AttachEngine3D
  Height = 59
  Length = 20
  Placement = pos=(-10,-53,26) rot=(0,0,1;0rad)
  Width = 17
FEATURE [Part::Cylinder] Cylinder1640  label="Válec1640"
  Angle = 360
  AttacherType = Attacher::AttachEngine3D
  Height = 40
  Placement = pos=(7,-34,37) rot=(1,0,0;1.5708rad)
  Radius = 1.5
FEATURE [Part::Box] Box658  label="Krychle658"
  AttacherType = Attacher::AttachEngine3D
  Height = 6
  Length = 8
  Placement = pos=(-11,-48,34) rot=(0,0,1;0rad)
  Width = 2
FEATURE [Part::Box] Box659  label="Krychle659"
  AttacherType = Attacher::AttachEngine3D
  Height = 100
  Length = 100
  Placement = pos=(-50,-41,0) rot=(0,0,1;0rad)
  Width = 5
FEATURE [Part::Cylinder] Cylinder1641  label="Válec1641"
  Angle = 360
  AttacherType = Attacher::AttachEngine3D
  Height = 40
  Placement = pos=(-7,-34,37) rot=(1,0,0;1.5708rad)
  Radius = 1.5
FEATURE [Part::Box] Box660  label="Krychle660"
  AttacherType = Attacher::AttachEngine3D
  Height = 6
  Length = 8
  Placement = pos=(3,-48,70) rot=(0,0,1;0rad)
  Width = 2
FEATURE [Part::Box] Box661  label="Krychle661"
  AttacherType = Attacher::AttachEngine3D
  Height = 6
  Length = 8
  Placement = pos=(3,-48,34) rot=(0,0,1;0rad)
  Width = 2
FEATURE [Part::Compound] Compound814
  Links = -> [Box661,Box658,Box660,Box656]
  Placement = pos=(0,-1,0) rot=(0,0,1;0rad)
FEATURE [Part::Compound] Compound815
  Links = -> [Cylinder1640,Cylinder1641,Cylinder1639,Cylinder1638]
  Placement = pos=(0,2,0) rot=(0,0,1;0rad)
FEATURE [Part::Cut] Cut191
  Base = -> Box657
  Tool = -> Compound815
FEATURE [Part::Cut] Cut192
  Base = -> Cut191
  Tool = -> Compound814
FEATURE [Part::Fillet] Fillet006
  Base = -> Cut192
  Edges = 2 edges r=8.9: [Edge2,Edge21]
FEATURE [Part::Common] Common  label="J-max_moto-hold-under-adaptor"
  Base = -> Fillet006
  Tool = -> Box659
FEATURE [Part::Cylinder] Cylinder1860  label="Válec1860"
  Angle = 360
  AttacherType = Attacher::AttachEngine3D
  Height = 20
  Placement = pos=(-23.55,-23.55,-34) rot=(0,0,1;0rad)
  Radius = 2.5
FEATURE [Part::Cylinder] Cylinder1862  label="Válec1862"
  Angle = 360
  AttacherType = Attacher::AttachEngine3D
  Height = 20
  Placement = pos=(-23.55,23.55,-34) rot=(0,0,1;0rad)
  Radius = 2.5
FEATURE [Part::Cylinder] Cylinder1861  label="Válec1861"
  Angle = 360
  AttacherType = Attacher::AttachEngine3D
  Height = 20
  Placement = pos=(23.55,23.55,-34) rot=(0,0,1;0rad)
  Radius = 2.5
FEATURE [Part::Cylinder] Cylinder1856  label="Válec1856"
  Angle = 360
  AttacherType = Attacher::AttachEngine3D
  Height = 1.75
  Placement = pos=(-23.55,-23.55,-34) rot=(0,0,1;0rad)
  Radius = 7
FEATURE [Part::Cylinder] Cylinder1857  label="Válec1857"
  Angle = 360
  AttacherType = Attacher::AttachEngine3D
  Height = 1.75
  Placement = pos=(23.55,23.55,-34) rot=(0,0,1;0rad)
  Radius = 7
FEATURE [Part::Cylinder] Cylinder1858  label="Válec1858"
  Angle = 360
  AttacherType = Attacher::AttachEngine3D
  Height = 1.75
  Placement = pos=(-23.55,23.55,-34) rot=(0,0,1;0rad)
  Radius = 7
FEATURE [Part::Cylinder] Cylinder1859  label="Válec1859"
  Angle = 360
  AttacherType = Attacher::AttachEngine3D
  Height = 20
  Placement = pos=(23.55,-23.55,-34) rot=(0,0,1;0rad)
  Radius = 2.5
FEATURE [Part::Compound] Compound930
  Links = -> [Cylinder1861,Cylinder1862,Cylinder1860,Cylinder1859]
  Placement = pos=(0,0,-8) rot=(0,0,1;0rad)
FEATURE [Part::Cylinder] Cylinder1855  label="Válec1855"
  Angle = 360
  AttacherType = Attacher::AttachEngine3D
  Height = 1.75
  Placement = pos=(23.55,-23.55,-34) rot=(0,0,1;0rad)
  Radius = 7
FEATURE [Part::Compound] Compound929
  Links = -> [Cylinder1857,Cylinder1858,Cylinder1856,Cylinder1855]
  Placement = pos=(0,0,-0.75) rot=(0,0,1;0rad)
FEATURE [Part::Cut] Cut318
  Base = -> Compound929
  Placement = pos=(0,0,68.75) rot=(1,0,0;0rad)
  Tool = -> Compound930
FEATURE [Part::Compound] Compound931  label="J-max_moto-hold"
  Links = -> [Chamfer060,Fillet004,Chamfer061,Fillet005,Cut318]
FEATURE [Mesh::Feature] Mesh006  label="J-max_moto-hold (Meshed)001"
